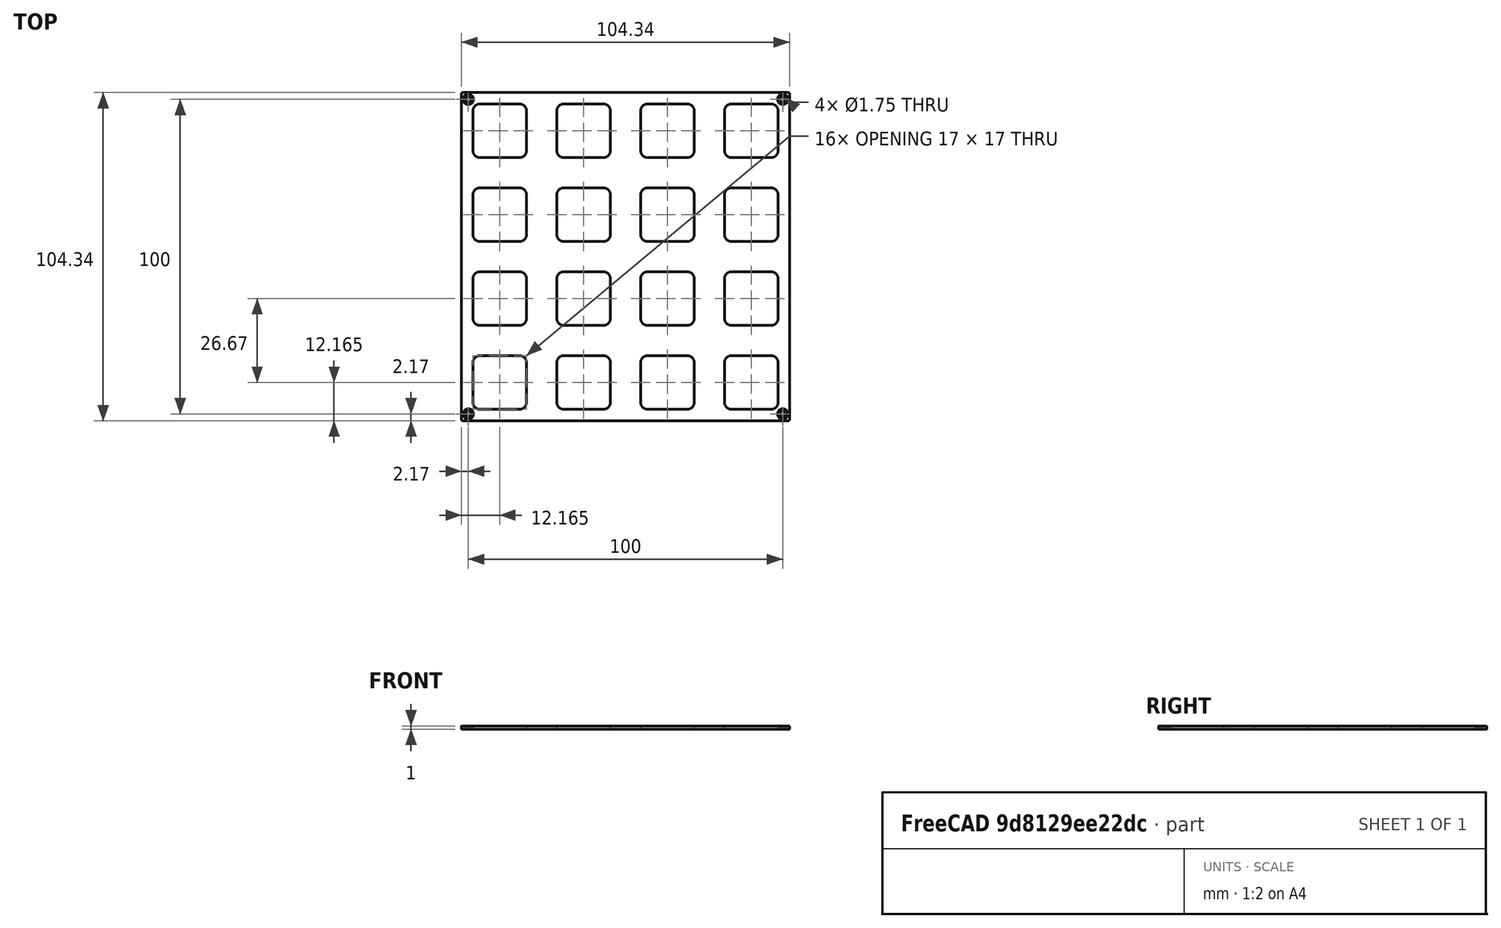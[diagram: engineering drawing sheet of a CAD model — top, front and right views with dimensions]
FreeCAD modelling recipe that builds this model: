
FCSTD DOCUMENT  (FreeCAD 1.0R39109 (Git))
Label: FRONTPANEL-SHEET-BU16 - VSN
License: All rights reserved
LicenseURL: https://en.wikipedia.org/wiki/All_rights_reserved
objects: TechDraw::DrawViewBalloon×13, TechDraw::DrawViewDimension×8, Sketcher::SketchObject×7, TechDraw::DrawHatch×7, TechDraw::DrawViewPart×5, TechDraw::DrawViewAnnotation×3, TechDraw::DrawSVGTemplate×2, PartDesign::Pocket×2, PartDesign::Body×2, TechDraw::DrawPage×2, Spreadsheet::Sheet×1, PartDesign::Pad×1, PartDesign::Hole×1, PartDesign::FeatureBase×1, TechDraw::DrawComplexSection×1
note: 41 computed .brp shape members not serialized (recipe doc carries the construction recipe); baked Part::Feature solids carry a one-line shape summary decoded from their .brp

FEATURE [TechDraw::DrawSVGTemplate] Template003
  EditableTexts = COLOR=Anodized matte black - RAL code: 9004; CreationDate=2024/05/14; E.G.APPROVED=APPROVED; FC-Scale=1:1; FC-Title=BU16 - frontpanel; IntechStudioLtd.=Intech Studio Ltd.; MATERIAL=Aluminum 5052-H32; REV=03; STANDARD=ISO 2768 - m
  Height = 297
  Orientation = 1
  Template = <userpath>/Desktop/A3_LandscapeTD_MODIFIED.svg
  Width = 420
FEATURE [Spreadsheet::Sheet] Spreadsheet  label="dim"
  cells = A1='panel_length; B1(panel_length)=104.35; A2='panel_thickness; B2(panel_thickness)=1; A3='panel_radius; B3(panel_radius)==(104.35 - 103.6) / 2; A5='corner_drill_dist; B5(corner_drill_dist)=100; A6='corner_drill_dia; B6(corner_drill_dia)=1.75; A7='corner_drill_countersink; B7(corner_drill_countersink)=3.3; A9='undercut_width; B9(undercut_width)=1; A10='undercut_length; B10(undercut_length)=90; A11='undercut_offset; B11(undercut_offset)=1; A12='undercut_depth; B12(undercut_depth)=0.8; A14='ui_raster; B14(ui_raster)=26.67; A16='light_drill_dia; B16(light_drill_dia)=3; D16='old 2.9; A17='light_bore_dia; B17(light_bore_dia)=3.45; C17='check; D17='old 3.30; E17='DEPRICATED; A18='light_bore_depth; B18(light_bore_depth)=0.4; C18='check; D18='old 0.40; E18='DEPRICATED; A20='pot_drill_dia; B20(pot_drill_dia)=9.7; C20='check; D20='old 6.20; A21='pot_led_dist; B21(pot_led_dist)=8.5; B22=0; A23='but_drill_dia; B23(but_drill_dia)=9.8; A24='but_led_dist; B24(but_led_dist)=8.5; A26='fad_cutout_width; B26(fad_cutout_width)=2; C26='check; D26='old 1.50; A27='fad_cutout_length; B27(fad_cutout_length)=36; A28='fad_led_dist; B28(fad_led_dist)=25; A30='enc_drill_dia; B30(enc_drill_dia)=9.7; C30='check; D30='old 6.20; A31='enc_led_dist; B31(enc_led_dist)=8.5; A33='longfad_cutout_width; B33(longfad_cutout_width)=2; A34='longfad_cutout_length; B34(longfad_cutout_length)=66; A36='panel_chamfer; B36(panel_chamfer)=0.2; C36='UPDATE DRAWING
FEATURE [Sketcher::SketchObject] Sketch006
  ArcFitTolerance = 0
  AttachmentSupport = -> [XY_Plane002]
  FullyConstrained = true
  MakeInternals = false
  MapMode = 5
  expr: Constraints[4] = <<dim>>.ui_raster
  expr: Constraints[84] = <<dim>>.but_led_dist
  sketch-geometry (34):
    g0: Circle CenterX=-40.005 CenterY=48.505 CenterZ=0 NormalX=0 NormalY=0 NormalZ=1 AngleXU=0 Radius=2
    g1: Circle CenterX=-13.335 CenterY=48.505 CenterZ=0 NormalX=0 NormalY=0 NormalZ=1 AngleXU=0 Radius=2
    g2: LineSegment [constr] StartX=-40.005 StartY=48.505 StartZ=0 EndX=-13.335 EndY=48.505 EndZ=0
    g3: Circle CenterX=13.335 CenterY=48.505 CenterZ=0 NormalX=0 NormalY=0 NormalZ=1 AngleXU=0 Radius=2
    g4: LineSegment [constr] StartX=-13.335 StartY=48.505 StartZ=0 EndX=13.335 EndY=48.505 EndZ=0
    g5: Circle CenterX=40.005 CenterY=48.505 CenterZ=0 NormalX=0 NormalY=0 NormalZ=1 AngleXU=0 Radius=2
    g6: LineSegment [constr] StartX=13.335 StartY=48.505 StartZ=0 EndX=40.005 EndY=48.505 EndZ=0
    g7: Circle CenterX=-40.005 CenterY=21.835 CenterZ=0 NormalX=0 NormalY=0 NormalZ=1 AngleXU=0 Radius=2
    g8: LineSegment [constr] StartX=-40.005 StartY=48.505 StartZ=0 EndX=-40.005 EndY=21.835 EndZ=0
    g9: Circle CenterX=-13.335 CenterY=21.835 CenterZ=0 NormalX=0 NormalY=0 NormalZ=1 AngleXU=0 Radius=2
    g10: LineSegment [constr] StartX=-40.005 StartY=21.835 StartZ=0 EndX=-13.335 EndY=21.835 EndZ=0
    g11: Circle CenterX=13.335 CenterY=21.835 CenterZ=0 NormalX=0 NormalY=0 NormalZ=1 AngleXU=0 Radius=2
    g12: LineSegment [constr] StartX=-13.335 StartY=21.835 StartZ=0 EndX=13.335 EndY=21.835 EndZ=0
    g13: Circle CenterX=40.005 CenterY=21.835 CenterZ=0 NormalX=0 NormalY=0 NormalZ=1 AngleXU=0 Radius=2
    g14: LineSegment [constr] StartX=13.335 StartY=21.835 StartZ=0 EndX=40.005 EndY=21.835 EndZ=0
    g15: Circle CenterX=-40.005 CenterY=-4.835 CenterZ=0 NormalX=0 NormalY=0 NormalZ=1 AngleXU=0 Radius=2
    g16: LineSegment [constr] StartX=-40.005 StartY=21.835 StartZ=0 EndX=-40.005 EndY=-4.835 EndZ=0
    g17: Circle CenterX=-13.335 CenterY=-4.835 CenterZ=0 NormalX=0 NormalY=0 NormalZ=1 AngleXU=0 Radius=2
    g18: LineSegment [constr] StartX=-40.005 StartY=-4.835 StartZ=0 EndX=-13.335 EndY=-4.835 EndZ=0
    g19: Circle CenterX=13.335 CenterY=-4.835 CenterZ=0 NormalX=0 NormalY=0 NormalZ=1 AngleXU=0 Radius=2
    g20: LineSegment [constr] StartX=-13.335 StartY=-4.835 StartZ=0 EndX=13.335 EndY=-4.835 EndZ=0
    g21: Circle CenterX=40.005 CenterY=-4.835 CenterZ=0 NormalX=0 NormalY=0 NormalZ=1 AngleXU=0 Radius=2
    g22: LineSegment [constr] StartX=13.335 StartY=-4.835 StartZ=0 EndX=40.005 EndY=-4.835 EndZ=0
    g23: Circle CenterX=-40.005 CenterY=-31.505 CenterZ=0 NormalX=0 NormalY=0 NormalZ=1 AngleXU=0 Radius=2
    g24: LineSegment [constr] StartX=-40.005 StartY=-4.835 StartZ=0 EndX=-40.005 EndY=-31.505 EndZ=0
    g25: Circle CenterX=-13.335 CenterY=-31.505 CenterZ=0 NormalX=0 NormalY=0 NormalZ=1 AngleXU=0 Radius=2
    g26: LineSegment [constr] StartX=-40.005 StartY=-31.505 StartZ=0 EndX=-13.335 EndY=-31.505 EndZ=0
    g27: Circle CenterX=13.335 CenterY=-31.505 CenterZ=0 NormalX=0 NormalY=0 NormalZ=1 AngleXU=0 Radius=2
    g28: LineSegment [constr] StartX=-13.335 StartY=-31.505 StartZ=0 EndX=13.335 EndY=-31.505 EndZ=0
    g29: Circle CenterX=40.005 CenterY=-31.505 CenterZ=0 NormalX=0 NormalY=0 NormalZ=1 AngleXU=0 Radius=2
    g30: LineSegment [constr] StartX=13.335 StartY=-31.505 StartZ=0 EndX=40.005 EndY=-31.505 EndZ=0
    g31: LineSegment [constr] StartX=-13.335 StartY=21.835 StartZ=0 EndX=-1.8e-15 EndY=8.5 EndZ=0
    g32: LineSegment [constr] StartX=-1.8e-15 StartY=8.5 StartZ=0 EndX=13.335 EndY=21.835 EndZ=0
    g33: LineSegment [constr] StartX=-1.8e-15 StartY=8.5 StartZ=0 EndX=-13.335 EndY=-4.835 EndZ=0
  constraints (85):
    c: Diameter(g0) = 4
    c: Diameter(g1) = 4
    c: Coincident(g0,g2)
    c: Coincident(g1,g2)
    c: Distance(g2) = 26.67
    c: Angle(g2) = 0
    c: Diameter(g3) = 4
    c: Coincident(g1,g4)
    c: Coincident(g3,g4)
    c: Equal(g2,g4)
    c: Parallel(g4,g2)
    c: Diameter(g5) = 4
    c: Coincident(g3,g6)
    c: Coincident(g5,g6)
    c: Equal(g2,g6)
    c: Parallel(g6,g2)
    c: Diameter(g7) = 4
    c: Coincident(g0,g8)
    c: Coincident(g7,g8)
    c: Equal(g8,g2)
    c: Perpendicular(g8,g2)
    c: Diameter(g9) = 4
    c: Coincident(g7,g10)
    c: Coincident(g9,g10)
    c: Equal(g2,g10)
    c: Parallel(g10,g2)
    c: Diameter(g11) = 4
    c: Coincident(g9,g12)
    c: Coincident(g11,g12)
    c: Equal(g2,g12)
    c: Parallel(g12,g2)
    c: Diameter(g13) = 4
    c: Coincident(g11,g14)
    c: Coincident(g13,g14)
    c: Equal(g2,g14)
    c: Parallel(g14,g2)
    c: Diameter(g15) = 4
    c: Coincident(g7,g16)
    c: Coincident(g15,g16)
    c: Equal(g8,g16)
    c: Perpendicular(g16,g2)
    c: Diameter(g17) = 4
    c: Coincident(g15,g18)
    c: Coincident(g17,g18)
    c: Equal(g2,g18)
    c: Parallel(g18,g2)
    c: Diameter(g19) = 4
    c: Coincident(g17,g20)
    c: Coincident(g19,g20)
    c: Equal(g2,g20)
    c: Parallel(g20,g2)
    c: Diameter(g21) = 4
    c: Coincident(g19,g22)
    c: Coincident(g21,g22)
    c: Equal(g2,g22)
    c: Parallel(g22,g2)
    c: Diameter(g23) = 4
    c: Coincident(g15,g24)
    c: Coincident(g23,g24)
    c: Equal(g8,g24)
    c: Perpendicular(g24,g2)
    c: Diameter(g25) = 4
    c: Coincident(g23,g26)
    c: Coincident(g25,g26)
    c: Equal(g2,g26)
    c: Parallel(g26,g2)
    c: Diameter(g27) = 4
    c: Coincident(g25,g28)
    c: Coincident(g27,g28)
    c: Equal(g2,g28)
    c: Parallel(g28,g2)
    c: Diameter(g29) = 4
    c: Coincident(g27,g30)
    c: Coincident(g29,g30)
    c: Equal(g2,g30)
    c: Parallel(g30,g2)
    c: Coincident(g31,g9)
    c: PointOnObject(g31,g-2)
    c: Coincident(g31,g32)
    c: Coincident(g32,g11)
    c: Coincident(g31,g33)
    c: Coincident(g33,g17)
    c: Equal(g33,g31)
    c: Equal(g31,g32)
    c: DistanceY(g-1,g31) = 8.5
FEATURE [Sketcher::SketchObject] Sketch005
  ArcFitTolerance = 0
  AttachmentSupport = -> [XY_Plane002]
  FullyConstrained = true
  MakeInternals = false
  MapMode = 5
  expr: Constraints[4] = <<dim>>.ui_raster
  sketch-geometry (34):
    g0: Circle CenterX=-40.005 CenterY=40.005 CenterZ=0 NormalX=0 NormalY=0 NormalZ=1 AngleXU=0 Radius=2
    g1: Circle CenterX=-13.335 CenterY=40.005 CenterZ=0 NormalX=0 NormalY=0 NormalZ=1 AngleXU=0 Radius=2
    g2: LineSegment [constr] StartX=-40.005 StartY=40.005 StartZ=0 EndX=-13.335 EndY=40.005 EndZ=0
    g3: Circle CenterX=13.335 CenterY=40.005 CenterZ=0 NormalX=0 NormalY=0 NormalZ=1 AngleXU=0 Radius=2
    g4: LineSegment [constr] StartX=-13.335 StartY=40.005 StartZ=0 EndX=13.335 EndY=40.005 EndZ=0
    g5: Circle CenterX=40.005 CenterY=40.005 CenterZ=0 NormalX=0 NormalY=0 NormalZ=1 AngleXU=0 Radius=2
    g6: LineSegment [constr] StartX=13.335 StartY=40.005 StartZ=0 EndX=40.005 EndY=40.005 EndZ=0
    g7: Circle CenterX=-40.005 CenterY=13.335 CenterZ=0 NormalX=0 NormalY=0 NormalZ=1 AngleXU=0 Radius=2
    g8: LineSegment [constr] StartX=-40.005 StartY=40.005 StartZ=0 EndX=-40.005 EndY=13.335 EndZ=0
    g9: Circle CenterX=-13.335 CenterY=13.335 CenterZ=0 NormalX=0 NormalY=0 NormalZ=1 AngleXU=0 Radius=2
    g10: LineSegment [constr] StartX=-40.005 StartY=13.335 StartZ=0 EndX=-13.335 EndY=13.335 EndZ=0
    g11: Circle CenterX=13.335 CenterY=13.335 CenterZ=0 NormalX=0 NormalY=0 NormalZ=1 AngleXU=0 Radius=2
    g12: LineSegment [constr] StartX=-13.335 StartY=13.335 StartZ=0 EndX=13.335 EndY=13.335 EndZ=0
    g13: Circle CenterX=40.005 CenterY=13.335 CenterZ=0 NormalX=0 NormalY=0 NormalZ=1 AngleXU=0 Radius=2
    g14: LineSegment [constr] StartX=13.335 StartY=13.335 StartZ=0 EndX=40.005 EndY=13.335 EndZ=0
    g15: Circle CenterX=-40.005 CenterY=-13.335 CenterZ=0 NormalX=0 NormalY=0 NormalZ=1 AngleXU=0 Radius=2
    g16: LineSegment [constr] StartX=-40.005 StartY=13.335 StartZ=0 EndX=-40.005 EndY=-13.335 EndZ=0
    g17: Circle CenterX=-13.335 CenterY=-13.335 CenterZ=0 NormalX=0 NormalY=0 NormalZ=1 AngleXU=0 Radius=2
    g18: LineSegment [constr] StartX=-40.005 StartY=-13.335 StartZ=0 EndX=-13.335 EndY=-13.335 EndZ=0
    g19: Circle CenterX=13.335 CenterY=-13.335 CenterZ=0 NormalX=0 NormalY=0 NormalZ=1 AngleXU=0 Radius=2
    g20: LineSegment [constr] StartX=-13.335 StartY=-13.335 StartZ=0 EndX=13.335 EndY=-13.335 EndZ=0
    g21: Circle CenterX=40.005 CenterY=-13.335 CenterZ=0 NormalX=0 NormalY=0 NormalZ=1 AngleXU=0 Radius=2
    g22: LineSegment [constr] StartX=13.335 StartY=-13.335 StartZ=0 EndX=40.005 EndY=-13.335 EndZ=0
    g23: Circle CenterX=-40.005 CenterY=-40.005 CenterZ=0 NormalX=0 NormalY=0 NormalZ=1 AngleXU=0 Radius=2
    g24: LineSegment [constr] StartX=-40.005 StartY=-13.335 StartZ=0 EndX=-40.005 EndY=-40.005 EndZ=0
    g25: Circle CenterX=-13.335 CenterY=-40.005 CenterZ=0 NormalX=0 NormalY=0 NormalZ=1 AngleXU=0 Radius=2
    g26: LineSegment [constr] StartX=-40.005 StartY=-40.005 StartZ=0 EndX=-13.335 EndY=-40.005 EndZ=0
    g27: Circle CenterX=13.335 CenterY=-40.005 CenterZ=0 NormalX=0 NormalY=0 NormalZ=1 AngleXU=0 Radius=2
    g28: LineSegment [constr] StartX=-13.335 StartY=-40.005 StartZ=0 EndX=13.335 EndY=-40.005 EndZ=0
    g29: Circle CenterX=40.005 CenterY=-40.005 CenterZ=0 NormalX=0 NormalY=0 NormalZ=1 AngleXU=0 Radius=2
    g30: LineSegment [constr] StartX=13.335 StartY=-40.005 StartZ=0 EndX=40.005 EndY=-40.005 EndZ=0
    g31: LineSegment [constr] StartX=-13.335 StartY=13.335 StartZ=0 EndX=-1.8e-15 EndY=0 EndZ=0
    g32: LineSegment [constr] StartX=-1.8e-15 StartY=0 StartZ=0 EndX=13.335 EndY=13.335 EndZ=0
    g33: LineSegment [constr] StartX=0 StartY=0 StartZ=0 EndX=-13.335 EndY=-13.335 EndZ=0
  constraints (84):
    c: Diameter(g0) = 4
    c: Diameter(g1) = 4
    c: Coincident(g0,g2)
    c: Coincident(g1,g2)
    c: Distance(g2) = 26.67
    c: Angle(g2) = 0
    c: Diameter(g3) = 4
    c: Coincident(g1,g4)
    c: Coincident(g3,g4)
    c: Equal(g2,g4)
    c: Parallel(g4,g2)
    c: Diameter(g5) = 4
    c: Coincident(g3,g6)
    c: Coincident(g5,g6)
    c: Equal(g2,g6)
    c: Parallel(g6,g2)
    c: Diameter(g7) = 4
    c: Coincident(g0,g8)
    c: Coincident(g7,g8)
    c: Equal(g8,g2)
    c: Perpendicular(g8,g2)
    c: Diameter(g9) = 4
    c: Coincident(g7,g10)
    c: Coincident(g9,g10)
    c: Equal(g2,g10)
    c: Parallel(g10,g2)
    c: Diameter(g11) = 4
    c: Coincident(g9,g12)
    c: Coincident(g11,g12)
    c: Equal(g2,g12)
    c: Parallel(g12,g2)
    c: Diameter(g13) = 4
    c: Coincident(g11,g14)
    c: Coincident(g13,g14)
    c: Equal(g2,g14)
    c: Parallel(g14,g2)
    c: Diameter(g15) = 4
    c: Coincident(g7,g16)
    c: Coincident(g15,g16)
    c: Equal(g8,g16)
    c: Perpendicular(g16,g2)
    c: Diameter(g17) = 4
    c: Coincident(g15,g18)
    c: Coincident(g17,g18)
    c: Equal(g2,g18)
    c: Parallel(g18,g2)
    c: Diameter(g19) = 4
    c: Coincident(g17,g20)
    c: Coincident(g19,g20)
    c: Equal(g2,g20)
    c: Parallel(g20,g2)
    c: Diameter(g21) = 4
    c: Coincident(g19,g22)
    c: Coincident(g21,g22)
    c: Equal(g2,g22)
    c: Parallel(g22,g2)
    c: Diameter(g23) = 4
    c: Coincident(g15,g24)
    c: Coincident(g23,g24)
    c: Equal(g8,g24)
    c: Perpendicular(g24,g2)
    c: Diameter(g25) = 4
    c: Coincident(g23,g26)
    c: Coincident(g25,g26)
    c: Equal(g2,g26)
    c: Parallel(g26,g2)
    c: Diameter(g27) = 4
    c: Coincident(g25,g28)
    c: Coincident(g27,g28)
    c: Equal(g2,g28)
    c: Parallel(g28,g2)
    c: Diameter(g29) = 4
    c: Coincident(g27,g30)
    c: Coincident(g29,g30)
    c: Equal(g2,g30)
    c: Parallel(g30,g2)
    c: Coincident(g31,g9)
    c: Coincident(g31,g-1)
    c: Coincident(g31,g32)
    c: Coincident(g32,g11)
    c: Coincident(g-1,g33)
    c: Coincident(g33,g17)
    c: Equal(g33,g31)
    c: Equal(g31,g32)
FEATURE [Sketcher::SketchObject] Sketch001
  ArcFitTolerance = 0
  AttachmentSupport = -> [XY_Plane]
  FullyConstrained = true
  MakeInternals = false
  MapMode = 5
  expr: Constraints[13] = <<dim>>.corner_drill_dist
  sketch-geometry (9):
    g0: LineSegment [constr] StartX=-50 StartY=50 StartZ=0 EndX=-50 EndY=-50 EndZ=0
    g1: LineSegment [constr] StartX=-50 StartY=-50 StartZ=0 EndX=50 EndY=-50 EndZ=0
    g2: LineSegment [constr] StartX=50 StartY=-50 StartZ=0 EndX=50 EndY=50 EndZ=0
    g3: LineSegment [constr] StartX=50 StartY=50 StartZ=0 EndX=-50 EndY=50 EndZ=0
    g4: Circle [constr] CenterX=0 CenterY=0 CenterZ=0 NormalX=0 NormalY=0 NormalZ=1 AngleXU=0 Radius=70.7107
    g5: Circle CenterX=-50 CenterY=50 CenterZ=0 NormalX=0 NormalY=0 NormalZ=1 AngleXU=0 Radius=0.5
    g6: Circle CenterX=50 CenterY=50 CenterZ=0 NormalX=0 NormalY=0 NormalZ=1 AngleXU=0 Radius=0.5
    g7: Circle CenterX=50 CenterY=-50 CenterZ=0 NormalX=0 NormalY=0 NormalZ=1 AngleXU=0 Radius=0.5
    g8: Circle CenterX=-50 CenterY=-50 CenterZ=0 NormalX=0 NormalY=0 NormalZ=1 AngleXU=0 Radius=0.5
  constraints (22):
    c: Coincident(g0,g1)
    c: Coincident(g1,g2)
    c: Coincident(g2,g3)
    c: Coincident(g3,g0)
    c: Equal(g0,g1)
    c: Equal(g0,g2)
    c: Equal(g0,g3)
    c: PointOnObject(g0,g4)
    c: PointOnObject(g1,g4)
    c: PointOnObject(g2,g4)
    c: PointOnObject(g3,g4)
    c: Coincident(g4,g-1)
    c: Horizontal(g3)
    c: DistanceX(g3,g3) = 100
    c: Coincident(g5,g0)
    c: Coincident(g6,g2)
    c: Coincident(g7,g1)
    c: Coincident(g8,g0)
    c: Diameter(g8) = 1
    c: Equal(g8,g7)
    c: Equal(g8,g6)
    c: Equal(g8,g5)
FEATURE [Sketcher::SketchObject] Sketch002
  ArcFitTolerance = 0
  AttachmentOffset = pos=(0,0,-4.8) rot=(0,0,1;0rad)
  AttachmentSupport = -> [XY_Plane]
  FullyConstrained = true
  MakeInternals = false
  MapMode = 5
  Placement = pos=(0,0,-4.8) rot=(0,0,1;0rad)
  expr: .AttachmentOffset.Base.z = -<<dim>>.undercut_depth - 4
  expr: Constraints[91] = <<dim>>.undercut_length
  expr: Constraints[92] = <<dim>>.undercut_width
  expr: Constraints[93] = <<dim>>.panel_length / 2 - <<dim>>.undercut_offset - <<dim>>.undercut_width / 2
  sketch-geometry (40):
    g0: LineSegment StartX=-45 StartY=50.175 StartZ=0 EndX=45 EndY=50.175 EndZ=0
    g1: LineSegment StartX=-45 StartY=51.175 StartZ=0 EndX=45 EndY=51.175 EndZ=0
    g2: LineSegment [constr] StartX=-50.675 StartY=45 StartZ=0 EndX=0 EndY=0 EndZ=0
    g3: LineSegment [constr] StartX=0 StartY=0 StartZ=0 EndX=-50.675 EndY=-45 EndZ=0
    g4: LineSegment [constr] StartX=0 StartY=0 StartZ=0 EndX=-45 EndY=50.675 EndZ=0
    g5: LineSegment [constr] StartX=45 StartY=50.675 StartZ=0 EndX=0 EndY=0 EndZ=0
    g6: LineSegment [constr] StartX=0 StartY=0 StartZ=0 EndX=50.675 EndY=45 EndZ=0
    g7: LineSegment [constr] StartX=50.675 StartY=-45 StartZ=0 EndX=0 EndY=0 EndZ=0
    g8: LineSegment [constr] StartX=0 StartY=0 StartZ=0 EndX=45 EndY=-50.675 EndZ=0
    g9: LineSegment [constr] StartX=0 StartY=0 StartZ=0 EndX=-45 EndY=-50.675 EndZ=0
    g10: ArcOfCircle CenterX=45 CenterY=50.675 CenterZ=0 NormalX=0 NormalY=0 NormalZ=1 AngleXU=0 Radius=0.5 StartAngle=4.71239 EndAngle=6.28319
    g11: ArcOfCircle CenterX=45 CenterY=50.675 CenterZ=0 NormalX=0 NormalY=0 NormalZ=1 AngleXU=0 Radius=0.5 StartAngle=0 EndAngle=1.5708
    g12: LineSegment [constr] StartX=45 StartY=50.675 StartZ=0 EndX=45.5 EndY=50.675 EndZ=0
    g13: ArcOfCircle CenterX=-45 CenterY=50.675 CenterZ=0 NormalX=0 NormalY=0 NormalZ=1 AngleXU=0 Radius=0.5 StartAngle=3.14159 EndAngle=4.71239
    g14: ArcOfCircle CenterX=-45 CenterY=50.675 CenterZ=0 NormalX=0 NormalY=0 NormalZ=1 AngleXU=0 Radius=0.5 StartAngle=1.5708 EndAngle=3.14159
    g15: LineSegment [constr] StartX=-45.5 StartY=50.675 StartZ=0 EndX=-45 EndY=50.675 EndZ=0
    g16: LineSegment StartX=-45 StartY=-51.175 StartZ=0 EndX=45 EndY=-51.175 EndZ=0
    g17: LineSegment StartX=-45 StartY=-50.175 StartZ=0 EndX=45 EndY=-50.175 EndZ=0
    g18: ArcOfCircle CenterX=45 CenterY=-50.675 CenterZ=0 NormalX=0 NormalY=0 NormalZ=1 AngleXU=0 Radius=0.5 StartAngle=4.71239 EndAngle=6.28319
    g19: ArcOfCircle CenterX=45 CenterY=-50.675 CenterZ=0 NormalX=0 NormalY=0 NormalZ=1 AngleXU=0 Radius=0.5 StartAngle=0 EndAngle=1.5708
    g20: LineSegment [constr] StartX=45 StartY=-50.675 StartZ=0 EndX=45.5 EndY=-50.675 EndZ=0
    g21: ArcOfCircle CenterX=-45 CenterY=-50.675 CenterZ=0 NormalX=0 NormalY=0 NormalZ=1 AngleXU=0 Radius=0.5 StartAngle=3.14159 EndAngle=4.71239
    g22: ArcOfCircle CenterX=-45 CenterY=-50.675 CenterZ=0 NormalX=0 NormalY=0 NormalZ=1 AngleXU=0 Radius=0.5 StartAngle=1.5708 EndAngle=3.14159
    g23: LineSegment [constr] StartX=-45.5 StartY=-50.675 StartZ=0 EndX=-45 EndY=-50.675 EndZ=0
    g24: LineSegment StartX=51.175 StartY=-45 StartZ=0 EndX=51.175 EndY=45 EndZ=0
    g25: LineSegment StartX=50.175 StartY=-45 StartZ=0 EndX=50.175 EndY=45 EndZ=0
    g26: ArcOfCircle CenterX=50.675 CenterY=45 CenterZ=0 NormalX=0 NormalY=0 NormalZ=1 AngleXU=0 Radius=0.5 StartAngle=3.8e-15 EndAngle=1.5708
    g27: ArcOfCircle CenterX=50.675 CenterY=45 CenterZ=0 NormalX=0 NormalY=0 NormalZ=1 AngleXU=0 Radius=0.5 StartAngle=1.5708 EndAngle=3.14159
    g28: LineSegment [constr] StartX=50.675 StartY=45 StartZ=0 EndX=50.675 EndY=45.5 EndZ=0
    g29: ArcOfCircle CenterX=50.675 CenterY=-45 CenterZ=0 NormalX=0 NormalY=0 NormalZ=1 AngleXU=0 Radius=0.5 StartAngle=4.71239 EndAngle=6.28319
    g30: ArcOfCircle CenterX=50.675 CenterY=-45 CenterZ=0 NormalX=0 NormalY=0 NormalZ=1 AngleXU=0 Radius=0.5 StartAngle=3.14159 EndAngle=4.71239
    g31: LineSegment [constr] StartX=50.675 StartY=-45.5 StartZ=0 EndX=50.675 EndY=-45 EndZ=0
    g32: LineSegment StartX=-50.175 StartY=-45 StartZ=0 EndX=-50.175 EndY=45 EndZ=0
    g33: LineSegment StartX=-51.175 StartY=-45 StartZ=0 EndX=-51.175 EndY=45 EndZ=0
    g34: ArcOfCircle CenterX=-50.675 CenterY=45 CenterZ=0 NormalX=0 NormalY=0 NormalZ=1 AngleXU=0 Radius=0.5 StartAngle=1.4e-15 EndAngle=1.5708
    g35: ArcOfCircle CenterX=-50.675 CenterY=45 CenterZ=0 NormalX=0 NormalY=0 NormalZ=1 AngleXU=0 Radius=0.5 StartAngle=1.5708 EndAngle=3.14159
    g36: LineSegment [constr] StartX=-50.675 StartY=45 StartZ=0 EndX=-50.675 EndY=45.5 EndZ=0
    g37: ArcOfCircle CenterX=-50.675 CenterY=-45 CenterZ=0 NormalX=0 NormalY=0 NormalZ=1 AngleXU=0 Radius=0.5 StartAngle=4.71239 EndAngle=6.28319
    g38: ArcOfCircle CenterX=-50.675 CenterY=-45 CenterZ=0 NormalX=0 NormalY=0 NormalZ=1 AngleXU=0 Radius=0.5 StartAngle=3.14159 EndAngle=4.71239
    g39: LineSegment [constr] StartX=-50.675 StartY=-45.5 StartZ=0 EndX=-50.675 EndY=-45 EndZ=0
  constraints (96):
    c: Horizontal(g0)
    c: Coincident(g2,g-1)
    c: Coincident(g2,g3)
    c: Coincident(g-1,g4)
    c: Coincident(g5,g-1)
    c: Coincident(g5,g6)
    c: Coincident(g7,g-1)
    c: Coincident(g7,g8)
    c: Coincident(g-1,g9)
    c: Equal(g5,g6)
    c: Equal(g6,g8)
    c: Equal(g8,g7)
    c: Equal(g7,g9)
    c: Equal(g9,g3)
    c: Equal(g3,g2)
    c: Equal(g2,g4)
    c: Coincident(g10,g5)
    c: Coincident(g11,g10)
    c: Coincident(g11,g10)
    c: Tangent(g11,g1) = 1.5708
    c: Tangent(g10,g0) = -1.5708
    c: Coincident(g12,g10)
    c: Coincident(g12,g10)
    c: Horizontal(g12)
    c: Coincident(g13,g4)
    c: Coincident(g14,g13)
    c: Coincident(g14,g13)
    c: Tangent(g14,g1) = 1.5708
    c: Tangent(g13,g0) = -1.5708
    c: Coincident(g15,g13)
    c: Coincident(g15,g13)
    c: Horizontal(g15)
    c: Horizontal(g1)
    c: Horizontal(g16)
    c: Coincident(g19,g18)
    c: Coincident(g19,g18)
    c: Tangent(g19,g17) = 1.5708
    c: Tangent(g18,g16) = -1.5708
    c: Coincident(g20,g18)
    c: Coincident(g20,g18)
    c: Horizontal(g20)
    c: Coincident(g22,g21)
    c: Coincident(g22,g21)
    c: Tangent(g22,g17) = 1.5708
    c: Tangent(g21,g16) = -1.5708
    c: Coincident(g23,g21)
    c: Coincident(g23,g21)
    c: Horizontal(g23)
    c: Horizontal(g17)
    c: Coincident(g21,g9)
    c: Coincident(g8,g18)
    c: Equal(g22,g14)
    c: Equal(g17,g1)
    c: Coincident(g27,g26)
    c: Coincident(g27,g26)
    c: Tangent(g27,g25) = 1.5708
    c: Tangent(g26,g24) = -1.5708
    c: Coincident(g28,g26)
    c: Coincident(g28,g26)
    c: Coincident(g30,g29)
    c: Coincident(g30,g29)
    c: Tangent(g30,g25) = 1.5708
    c: Tangent(g29,g24) = -1.5708
    c: Coincident(g31,g29)
    c: Coincident(g31,g29)
    c: Vertical(g31)
    c: Vertical(g28)
    c: Vertical(g25)
    c: Vertical(g24)
    c: Coincident(g35,g34)
    c: Coincident(g35,g34)
    c: Tangent(g35,g33) = 1.5708
    c: Tangent(g34,g32) = -1.5708
    c: Coincident(g36,g34)
    c: Coincident(g36,g34)
    c: Coincident(g38,g37)
    c: Coincident(g38,g37)
    c: Tangent(g38,g33) = 1.5708
    c: Tangent(g37,g32) = -1.5708
    c: Coincident(g39,g37)
    c: Coincident(g39,g37)
    c: Vertical(g39)
    c: Vertical(g36)
    c: Vertical(g33)
    c: Vertical(g32)
    c: Coincident(g6,g26)
    c: Coincident(g7,g29)
    c: Equal(g25,g0)
    c: Equal(g11,g27)
    c: Equal(g1,g33)
    c: Equal(g35,g11)
    c: DistanceX(g13,g10) = 90
    c: Diameter(g13) = 1
    c: DistanceY(g-1,g13) = 50.675
    c: Coincident(g2,g34)
    c: Coincident(g3,g37)
FEATURE [Sketcher::SketchObject] Sketch
  ArcFitTolerance = 0
  AttachmentSupport = -> [XY_Plane]
  FullyConstrained = true
  MakeInternals = false
  MapMode = 5
  expr: Constraints[12] = <<dim>>.panel_radius
  expr: Constraints[16] = <<dim>>.panel_length
  sketch-geometry (11):
    g0: LineSegment StartX=-51.8 StartY=52.175 StartZ=0 EndX=51.8 EndY=52.175 EndZ=0
    g1: LineSegment StartX=52.175 StartY=51.8 StartZ=0 EndX=52.175 EndY=-51.8 EndZ=0
    g2: LineSegment StartX=51.8 StartY=-52.175 StartZ=0 EndX=-51.8 EndY=-52.175 EndZ=0
    g3: LineSegment StartX=-52.175 StartY=-51.8 StartZ=0 EndX=-52.175 EndY=51.8 EndZ=0
    g4: ArcOfCircle CenterX=-51.8 CenterY=51.8 CenterZ=0 NormalX=0 NormalY=0 NormalZ=1 AngleXU=0 Radius=0.375 StartAngle=1.5708 EndAngle=3.14159
    g5: ArcOfCircle CenterX=51.8 CenterY=51.8 CenterZ=0 NormalX=0 NormalY=0 NormalZ=1 AngleXU=0 Radius=0.375 StartAngle=8.4e-15 EndAngle=1.5708
    g6: ArcOfCircle CenterX=51.8 CenterY=-51.8 CenterZ=0 NormalX=0 NormalY=0 NormalZ=1 AngleXU=0 Radius=0.375 StartAngle=4.71239 EndAngle=6.28319
    g7: ArcOfCircle CenterX=-51.8 CenterY=-51.8 CenterZ=0 NormalX=0 NormalY=0 NormalZ=1 AngleXU=0 Radius=0.375 StartAngle=3.14159 EndAngle=4.71239
    g8: LineSegment [constr] StartX=-51.8 StartY=51.8 StartZ=0 EndX=0 EndY=0 EndZ=0
    g9: LineSegment [constr] StartX=0 StartY=0 StartZ=0 EndX=51.8 EndY=51.8 EndZ=0
    g10: LineSegment [constr] StartX=0 StartY=0 StartZ=0 EndX=-51.8 EndY=-51.8 EndZ=0
  constraints (26):
    c: Horizontal(g0)
    c: Horizontal(g2)
    c: Vertical(g1)
    c: Vertical(g3)
    c: Tangent(g3,g4) = 1.5708
    c: Tangent(g0,g4) = 1.5708
    c: Tangent(g0,g5) = 1.5708
    c: Tangent(g1,g5) = 1.5708
    c: Tangent(g1,g6) = 1.5708
    c: Tangent(g2,g6) = 1.5708
    c: Tangent(g2,g7) = 1.5708
    c: Tangent(g3,g7) = 1.5708
    c: Radius(g4) = 0.375
    c: Equal(g4,g5)
    c: Equal(g4,g6)
    c: Equal(g4,g7)
    c: DistanceX(g3,g1) = 104.35
    c: Equal(g3,g0)
    c: Coincident(g8,g4)
    c: Coincident(g8,g-1)
    c: Coincident(g8,g9)
    c: Coincident(g9,g5)
    c: Coincident(g-1,g10)
    c: Coincident(g10,g7)
    c: Equal(g10,g8)
    c: Equal(g8,g9)
FEATURE [PartDesign::Pad] Pad  label="panel"
  AllowMultiFace = false
  Direction = (0,0,1)
  Length = 1
  Length2 = 100
  Profile = -> Sketch
  Reversed = true
  Suppressed = false
  Type = 0
  expr: Length = <<dim>>.panel_thickness
FEATURE [PartDesign::Pocket] Pocket
  AllowMultiFace = false
  BaseFeature = -> Pad
  Direction = (0,0,-1)
  Length = 5
  Length2 = 100
  Profile = -> Sketch002
  Suppressed = false
  Type = 1
FEATURE [PartDesign::Hole] Hole
  BaseFeature = -> Pocket
  CustomThreadClearance = 0
  Depth = 298.105
  DepthType = 1
  Diameter = 1.75
  DrillForDepth = false
  DrillPoint = 1
  DrillPointAngle = 118
  HoleCutCountersinkAngle = 90
  HoleCutCustomValues = false
  HoleCutDepth = 0
  HoleCutDiameter = 3.3
  HoleCutType = 2
  ModelThread = false
  Profile = -> Sketch001
  Suppressed = false
  Tapered = false
  TaperedAngle = 90
  ThreadClass = 0
  ThreadDepth = 298.105
  ThreadDepthType = 0
  ThreadDirection = 0
  ThreadFit = 0
  ThreadSize = 0
  ThreadType = 0
  Threaded = false
  UseCustomThreadClearance = false
  expr: Diameter = <<dim>>.corner_drill_dia
  expr: HoleCutDiameter = <<dim>>.corner_drill_countersink
FEATURE [PartDesign::Body] Body  label="Base"
  AllowCompound = false
  Group = -> [Sketch,Pad,Sketch001,Sketch002,Pocket,Hole]
  Origin = -> Origin
  Tip = -> Hole
FEATURE [PartDesign::FeatureBase] Clone001
  BaseFeature = -> Body
  Suppressed = false
FEATURE [TechDraw::DrawViewAnnotation] Annotation
  Font = osifont
  LineSpace = 100
  LockPosition = false
  MaxWidth = -1
  Rotation = 0
  ScaleType = 0
  Text = 10:1
  TextSize = 4
  TextStyle = 0
  X = 76.4884
  Y = 42.7227
FEATURE [TechDraw::DrawViewAnnotation] Annotation001
  Font = osifont
  LineSpace = 100
  LockPosition = false
  MaxWidth = -1
  Rotation = 0
  ScaleType = 0
  Text = 1:2
  TextSize = 4
  TextStyle = 0
  X = 380.038
  Y = 120.843
FEATURE [Sketcher::SketchObject] Sketch007  label="Section A-A"
  ArcFitTolerance = 0
  AttachmentSupport = -> [XY_Plane002]
  FullyConstrained = true
  MakeInternals = false
  MapMode = 5
  sketch-geometry (2):
    g0: LineSegment StartX=-53.5 StartY=-50 StartZ=0 EndX=-46.5 EndY=-50 EndZ=0
    g1: GeomPoint X=-50 Y=-50 Z=0
  constraints (5):
    c: Horizontal(g0)
    c: DistanceX(g0,g0) = 7
    c: Symmetric(g0,g0,g1)
    c: DistanceY(g1,g-1) = 50
    c: DistanceX(g1,g-1) = 50
FEATURE [TechDraw::DrawViewAnnotation] Annotation002
  Font = osifont
  LineSpace = 100
  LockPosition = false
  MaxWidth = -1
  Rotation = 0
  ScaleType = 0
  Text = The mid of the datum plane A is preferred to be near | to the lower limit of the flatness tolerance zone. | It can be achieved with an additional bending step. | Aesthetical surfaces colored red on the view | No scratches, burrs or any kind of damage allowed! | Functional surfaces colored blue on the view (all which perpendicular to the aesthetical) | No burrs or other protruding material allowed!
  TextSize = 3
  TextStyle = 0
  X = 297.303
  Y = 101.437
FEATURE [TechDraw::DrawSVGTemplate] Template
  Height = 210
  Orientation = 1
  Template = C:/Program Files/FreeCAD 0.21/data/Mod/TechDraw/Templates/A4_Landscape_blank.svg
  Width = 297
FEATURE [TechDraw::DrawViewPart] View005
  CoarseView = false
  Direction = (0,0,1)
  Focus = 100
  HardHidden = false
  IsoCount = 0
  IsoHidden = false
  IsoVisible = true
  LockPosition = false
  Perspective = false
  Rotation = 0
  ScaleType = 0
  ScrubCount = 0
  SeamHidden = false
  SeamVisible = true
  SmoothHidden = false
  SmoothVisible = true
  X = 148.5
  XDirection = (1,0,0)
  Y = 105
FEATURE [TechDraw::DrawPage] Page  label="BU16_dxf"
  KeepUpdated = true
  NextBalloonIndex = 1
  ProjectionType = 0
  Template = -> Template
  Views = -> [View005]
FEATURE [TechDraw::DrawViewBalloon] Balloon026
  BubbleShape = 2
  EndType = 6
  EndTypeScale = 1
  KinkLength = 0
  LockPosition = false
  OriginX = -97.7934
  OriginY = -2.76733
  Rotation = 0
  ScaleType = 0
  ShapeScale = 1
  SourceView = -> Annotation002
  Text = 3
  TextWrapLen = -1
  X = -94.5881
  Y = -3.56147
FEATURE [Sketcher::SketchObject] Sketch008
  ArcFitTolerance = 1e-06
  AttachmentSupport = -> [XY_Plane002]
  FullyConstrained = true
  MakeInternals = false
  MapMode = 5
  sketch-geometry (264):
    g0: LineSegment StartX=33.605 StartY=31.505 StartZ=0 EndX=46.405 EndY=31.505 EndZ=0
    g1: LineSegment StartX=48.505 StartY=33.605 StartZ=0 EndX=48.505 EndY=46.405 EndZ=0
    g2: LineSegment StartX=46.405 StartY=48.505 StartZ=0 EndX=33.605 EndY=48.505 EndZ=0
    g3: LineSegment StartX=31.505 StartY=46.405 StartZ=0 EndX=31.505 EndY=33.605 EndZ=0
    g4: ArcOfCircle CenterX=33.605 CenterY=46.405 CenterZ=0 NormalX=0 NormalY=0 NormalZ=1 AngleXU=0 Radius=2.1 StartAngle=1.5708 EndAngle=3.14159
    g5: GeomPoint [constr] X=31.505 Y=48.505 Z=0
    g6: ArcOfCircle CenterX=46.405 CenterY=33.605 CenterZ=0 NormalX=0 NormalY=0 NormalZ=1 AngleXU=0 Radius=2.1 StartAngle=4.71239 EndAngle=6.28319
    g7: GeomPoint [constr] X=48.505 Y=31.505 Z=0
    g8: ArcOfCircle CenterX=46.405 CenterY=46.405 CenterZ=0 NormalX=0 NormalY=0 NormalZ=1 AngleXU=0 Radius=2.1 StartAngle=9e-16 EndAngle=1.5708
    g9: GeomPoint [constr] X=48.505 Y=48.505 Z=0
    g10: ArcOfCircle CenterX=33.605 CenterY=33.605 CenterZ=0 NormalX=0 NormalY=0 NormalZ=1 AngleXU=0 Radius=2.1 StartAngle=3.14159 EndAngle=4.71239
    g11: GeomPoint [constr] X=31.505 Y=31.505 Z=0
    g12: GeomPoint X=40.005 Y=40.005 Z=0
    g13: LineSegment [constr] StartX=40.005 StartY=48.505 StartZ=0 EndX=40.005 EndY=31.505 EndZ=0
    g14: LineSegment [constr] StartX=31.505 StartY=40.005 StartZ=0 EndX=48.505 EndY=40.005 EndZ=0
    g15: LineSegment [constr] StartX=-40.005 StartY=13.335 StartZ=0 EndX=-13.335 EndY=13.335 EndZ=0
    g16: LineSegment [constr] StartX=-13.335 StartY=13.335 StartZ=0 EndX=-13.335 EndY=40.005 EndZ=0
    g17: LineSegment [constr] StartX=-13.335 StartY=40.005 StartZ=0 EndX=-40.005 EndY=40.005 EndZ=0
    g18: LineSegment [constr] StartX=-40.005 StartY=40.005 StartZ=0 EndX=-40.005 EndY=13.335 EndZ=0
    g19: LineSegment [constr] StartX=13.335 StartY=13.335 StartZ=0 EndX=40.005 EndY=13.335 EndZ=0
    g20: LineSegment [constr] StartX=40.005 StartY=13.335 StartZ=0 EndX=40.005 EndY=40.005 EndZ=0
    g21: LineSegment [constr] StartX=40.005 StartY=40.005 StartZ=0 EndX=13.335 EndY=40.005 EndZ=0
    g22: LineSegment [constr] StartX=13.335 StartY=40.005 StartZ=0 EndX=13.335 EndY=13.335 EndZ=0
    g23: LineSegment [constr] StartX=-13.335 StartY=40.005 StartZ=0 EndX=13.335 EndY=40.005 EndZ=0
    g24: LineSegment [constr] StartX=13.335 StartY=13.335 StartZ=0 EndX=-13.335 EndY=13.335 EndZ=0
    g25: LineSegment [constr] StartX=-40.005 StartY=-13.335 StartZ=0 EndX=-40.005 EndY=-40.005 EndZ=0
    g26: LineSegment [constr] StartX=-40.005 StartY=-40.005 StartZ=0 EndX=-13.335 EndY=-40.005 EndZ=0
    g27: LineSegment [constr] StartX=-13.335 StartY=-40.005 StartZ=0 EndX=-13.335 EndY=-13.335 EndZ=0
    g28: LineSegment [constr] StartX=-13.335 StartY=-13.335 StartZ=0 EndX=-40.005 EndY=-13.335 EndZ=0
    g29: LineSegment [constr] StartX=13.335 StartY=-13.335 StartZ=0 EndX=13.335 EndY=-40.005 EndZ=0
    g30: LineSegment [constr] StartX=13.335 StartY=-40.005 StartZ=0 EndX=40.005 EndY=-40.005 EndZ=0
    g31: LineSegment [constr] StartX=40.005 StartY=-40.005 StartZ=0 EndX=40.005 EndY=-13.335 EndZ=0
    g32: LineSegment [constr] StartX=40.005 StartY=-13.335 StartZ=0 EndX=13.335 EndY=-13.335 EndZ=0
    g33: LineSegment [constr] StartX=-40.005 StartY=13.335 StartZ=0 EndX=-40.005 EndY=-13.335 EndZ=0
    g34: LineSegment [constr] StartX=-13.335 StartY=13.335 StartZ=0 EndX=-13.335 EndY=-13.335 EndZ=0
    g35: LineSegment [constr] StartX=-13.335 StartY=-13.335 StartZ=0 EndX=13.335 EndY=-13.335 EndZ=0
    g36: LineSegment [constr] StartX=13.335 StartY=13.335 StartZ=0 EndX=13.335 EndY=-13.335 EndZ=0
    g37: LineSegment [constr] StartX=40.005 StartY=13.335 StartZ=0 EndX=40.005 EndY=-13.335 EndZ=0
    g38: LineSegment [constr] StartX=13.335 StartY=-40.005 StartZ=0 EndX=-13.335 EndY=-40.005 EndZ=0
    g39: LineSegment StartX=-19.735 StartY=31.505 StartZ=0 EndX=-6.935 EndY=31.505 EndZ=0
    g40: LineSegment StartX=-4.835 StartY=33.605 StartZ=0 EndX=-4.835 EndY=46.405 EndZ=0
    g41: LineSegment StartX=-6.935 StartY=48.505 StartZ=0 EndX=-19.735 EndY=48.505 EndZ=0
    g42: LineSegment StartX=-21.835 StartY=46.405 StartZ=0 EndX=-21.835 EndY=33.605 EndZ=0
    g43: ArcOfCircle CenterX=-19.735 CenterY=46.405 CenterZ=0 NormalX=0 NormalY=0 NormalZ=1 AngleXU=0 Radius=2.1 StartAngle=1.5708 EndAngle=3.14159
    g44: GeomPoint [constr] X=-21.835 Y=48.505 Z=0
    g45: ArcOfCircle CenterX=-6.935 CenterY=33.605 CenterZ=0 NormalX=0 NormalY=0 NormalZ=1 AngleXU=0 Radius=2.1 StartAngle=4.71239 EndAngle=6.28319
    g46: GeomPoint [constr] X=-4.835 Y=31.505 Z=0
    g47: ArcOfCircle CenterX=-6.935 CenterY=46.405 CenterZ=0 NormalX=0 NormalY=0 NormalZ=1 AngleXU=0 Radius=2.1 StartAngle=-9e-16 EndAngle=1.5708
    g48: GeomPoint [constr] X=-4.835 Y=48.505 Z=0
    g49: ArcOfCircle CenterX=-19.735 CenterY=33.605 CenterZ=0 NormalX=0 NormalY=0 NormalZ=1 AngleXU=0 Radius=2.1 StartAngle=3.14159 EndAngle=4.71239
    g50: GeomPoint [constr] X=-21.835 Y=31.505 Z=0
    g51: GeomPoint X=-13.335 Y=40.005 Z=0
    g52: LineSegment [constr] StartX=-13.335 StartY=48.505 StartZ=0 EndX=-13.335 EndY=31.505 EndZ=0
    g53: LineSegment [constr] StartX=-21.835 StartY=40.005 StartZ=0 EndX=-4.835 EndY=40.005 EndZ=0
    g54: LineSegment StartX=6.935 StartY=31.505 StartZ=0 EndX=19.735 EndY=31.505 EndZ=0
    g55: LineSegment StartX=21.835 StartY=33.605 StartZ=0 EndX=21.835 EndY=46.405 EndZ=0
    g56: LineSegment StartX=19.735 StartY=48.505 StartZ=0 EndX=6.935 EndY=48.505 EndZ=0
    g57: LineSegment StartX=4.835 StartY=46.405 StartZ=0 EndX=4.835 EndY=33.605 EndZ=0
    g58: ArcOfCircle CenterX=6.935 CenterY=46.405 CenterZ=0 NormalX=0 NormalY=0 NormalZ=1 AngleXU=0 Radius=2.1 StartAngle=1.5708 EndAngle=3.14159
    g59: GeomPoint [constr] X=4.835 Y=48.505 Z=0
    g60: ArcOfCircle CenterX=19.735 CenterY=33.605 CenterZ=0 NormalX=0 NormalY=0 NormalZ=1 AngleXU=0 Radius=2.1 StartAngle=4.71239 EndAngle=6.28319
    g61: GeomPoint [constr] X=21.835 Y=31.505 Z=0
    g62: ArcOfCircle CenterX=19.735 CenterY=46.405 CenterZ=0 NormalX=0 NormalY=0 NormalZ=1 AngleXU=0 Radius=2.1 StartAngle=2e-16 EndAngle=1.5708
    g63: GeomPoint [constr] X=21.835 Y=48.505 Z=0
    g64: ArcOfCircle CenterX=6.935 CenterY=33.605 CenterZ=0 NormalX=0 NormalY=0 NormalZ=1 AngleXU=0 Radius=2.1 StartAngle=3.14159 EndAngle=4.71239
    g65: GeomPoint [constr] X=4.835 Y=31.505 Z=0
    g66: GeomPoint X=13.335 Y=40.005 Z=0
    g67: LineSegment [constr] StartX=13.335 StartY=48.505 StartZ=0 EndX=13.335 EndY=31.505 EndZ=0
    g68: LineSegment [constr] StartX=4.835 StartY=40.005 StartZ=0 EndX=21.835 EndY=40.005 EndZ=0
    g69: LineSegment StartX=33.605 StartY=4.835 StartZ=0 EndX=46.405 EndY=4.835 EndZ=0
    g70: LineSegment StartX=48.505 StartY=6.935 StartZ=0 EndX=48.505 EndY=19.735 EndZ=0
    g71: LineSegment StartX=46.405 StartY=21.835 StartZ=0 EndX=33.605 EndY=21.835 EndZ=0
    g72: LineSegment StartX=31.505 StartY=19.735 StartZ=0 EndX=31.505 EndY=6.935 EndZ=0
    g73: ArcOfCircle CenterX=33.605 CenterY=19.735 CenterZ=0 NormalX=0 NormalY=0 NormalZ=1 AngleXU=0 Radius=2.1 StartAngle=1.5708 EndAngle=3.14159
    g74: GeomPoint [constr] X=31.505 Y=21.835 Z=0
    g75: ArcOfCircle CenterX=46.405 CenterY=6.935 CenterZ=0 NormalX=0 NormalY=0 NormalZ=1 AngleXU=0 Radius=2.1 StartAngle=4.71239 EndAngle=6.28319
    g76: GeomPoint [constr] X=48.505 Y=4.835 Z=0
    g77: ArcOfCircle CenterX=46.405 CenterY=19.735 CenterZ=0 NormalX=0 NormalY=0 NormalZ=1 AngleXU=0 Radius=2.1 StartAngle=4e-16 EndAngle=1.5708
    g78: GeomPoint [constr] X=48.505 Y=21.835 Z=0
    g79: ArcOfCircle CenterX=33.605 CenterY=6.935 CenterZ=0 NormalX=0 NormalY=0 NormalZ=1 AngleXU=0 Radius=2.1 StartAngle=3.14159 EndAngle=4.71239
    g80: GeomPoint [constr] X=31.505 Y=4.835 Z=0
    g81: GeomPoint X=40.005 Y=13.335 Z=0
    g82: LineSegment [constr] StartX=40.005 StartY=21.835 StartZ=0 EndX=40.005 EndY=4.835 EndZ=0
    g83: LineSegment [constr] StartX=31.505 StartY=13.335 StartZ=0 EndX=48.505 EndY=13.335 EndZ=0
    g84: LineSegment StartX=6.935 StartY=4.835 StartZ=0 EndX=19.735 EndY=4.835 EndZ=0
    g85: LineSegment StartX=21.835 StartY=6.935 StartZ=0 EndX=21.835 EndY=19.735 EndZ=0
    g86: LineSegment StartX=19.735 StartY=21.835 StartZ=0 EndX=6.935 EndY=21.835 EndZ=0
    g87: LineSegment StartX=4.835 StartY=19.735 StartZ=0 EndX=4.835 EndY=6.935 EndZ=0
    g88: ArcOfCircle CenterX=6.935 CenterY=19.735 CenterZ=0 NormalX=0 NormalY=0 NormalZ=1 AngleXU=0 Radius=2.1 StartAngle=1.5708 EndAngle=3.14159
    g89: GeomPoint [constr] X=4.835 Y=21.835 Z=0
    g90: ArcOfCircle CenterX=19.735 CenterY=6.935 CenterZ=0 NormalX=0 NormalY=0 NormalZ=1 AngleXU=0 Radius=2.1 StartAngle=4.71239 EndAngle=6.28319
    g91: GeomPoint [constr] X=21.835 Y=4.835 Z=0
    g92: ArcOfCircle CenterX=19.735 CenterY=19.735 CenterZ=0 NormalX=0 NormalY=0 NormalZ=1 AngleXU=0 Radius=2.1 StartAngle=0 EndAngle=1.5708
    g93: GeomPoint [constr] X=21.835 Y=21.835 Z=0
    g94: ArcOfCircle CenterX=6.935 CenterY=6.935 CenterZ=0 NormalX=0 NormalY=0 NormalZ=1 AngleXU=0 Radius=2.1 StartAngle=3.14159 EndAngle=4.71239
    g95: GeomPoint [constr] X=4.835 Y=4.835 Z=0
    g96: GeomPoint X=13.335 Y=13.335 Z=0
    g97: LineSegment [constr] StartX=13.335 StartY=21.835 StartZ=0 EndX=13.335 EndY=4.835 EndZ=0
    g98: LineSegment [constr] StartX=4.835 StartY=13.335 StartZ=0 EndX=21.835 EndY=13.335 EndZ=0
    g99: LineSegment StartX=-19.735 StartY=4.835 StartZ=0 EndX=-6.935 EndY=4.835 EndZ=0
    g100: LineSegment StartX=-4.835 StartY=6.935 StartZ=0 EndX=-4.835 EndY=19.735 EndZ=0
    g101: LineSegment StartX=-6.935 StartY=21.835 StartZ=0 EndX=-19.735 EndY=21.835 EndZ=0
    g102: LineSegment StartX=-21.835 StartY=19.735 StartZ=0 EndX=-21.835 EndY=6.935 EndZ=0
    g103: ArcOfCircle CenterX=-19.735 CenterY=19.735 CenterZ=0 NormalX=0 NormalY=0 NormalZ=1 AngleXU=0 Radius=2.1 StartAngle=1.5708 EndAngle=3.14159
    g104: GeomPoint [constr] X=-21.835 Y=21.835 Z=0
    g105: ArcOfCircle CenterX=-6.935 CenterY=6.935 CenterZ=0 NormalX=0 NormalY=0 NormalZ=1 AngleXU=0 Radius=2.1 StartAngle=4.71239 EndAngle=6.28319
    g106: GeomPoint [constr] X=-4.835 Y=4.835 Z=0
    g107: ArcOfCircle CenterX=-6.935 CenterY=19.735 CenterZ=0 NormalX=0 NormalY=0 NormalZ=1 AngleXU=0 Radius=2.1 StartAngle=0 EndAngle=1.5708
    g108: GeomPoint [constr] X=-4.835 Y=21.835 Z=0
    g109: ArcOfCircle CenterX=-19.735 CenterY=6.935 CenterZ=0 NormalX=0 NormalY=0 NormalZ=1 AngleXU=0 Radius=2.1 StartAngle=3.14159 EndAngle=4.71239
    g110: GeomPoint [constr] X=-21.835 Y=4.835 Z=0
    g111: GeomPoint X=-13.335 Y=13.335 Z=0
    g112: LineSegment [constr] StartX=-13.335 StartY=21.835 StartZ=0 EndX=-13.335 EndY=4.835 EndZ=0
    g113: LineSegment [constr] StartX=-21.835 StartY=13.335 StartZ=0 EndX=-4.835 EndY=13.335 EndZ=0
    g114: LineSegment StartX=-46.405 StartY=4.835 StartZ=0 EndX=-33.605 EndY=4.835 EndZ=0
    g115: LineSegment StartX=-31.505 StartY=6.935 StartZ=0 EndX=-31.505 EndY=19.735 EndZ=0
    g116: LineSegment StartX=-33.605 StartY=21.835 StartZ=0 EndX=-46.405 EndY=21.835 EndZ=0
    g117: LineSegment StartX=-48.505 StartY=19.735 StartZ=0 EndX=-48.505 EndY=6.935 EndZ=0
    g118: ArcOfCircle CenterX=-46.405 CenterY=19.735 CenterZ=0 NormalX=0 NormalY=0 NormalZ=1 AngleXU=0 Radius=2.1 StartAngle=1.5708 EndAngle=3.14159
    g119: GeomPoint [constr] X=-48.505 Y=21.835 Z=0
    g120: ArcOfCircle CenterX=-33.605 CenterY=6.935 CenterZ=0 NormalX=0 NormalY=0 NormalZ=1 AngleXU=0 Radius=2.1 StartAngle=4.71239 EndAngle=6.28319
    g121: GeomPoint [constr] X=-31.505 Y=4.835 Z=0
    g122: ArcOfCircle CenterX=-33.605 CenterY=19.735 CenterZ=0 NormalX=0 NormalY=0 NormalZ=1 AngleXU=0 Radius=2.1 StartAngle=0 EndAngle=1.5708
    g123: GeomPoint [constr] X=-31.505 Y=21.835 Z=0
    g124: ArcOfCircle CenterX=-46.405 CenterY=6.935 CenterZ=0 NormalX=0 NormalY=0 NormalZ=1 AngleXU=0 Radius=2.1 StartAngle=3.14159 EndAngle=4.71239
    g125: GeomPoint [constr] X=-48.505 Y=4.835 Z=0
    g126: GeomPoint X=-40.005 Y=13.335 Z=0
    g127: LineSegment [constr] StartX=-40.005 StartY=21.835 StartZ=0 EndX=-40.005 EndY=4.835 EndZ=0
    g128: LineSegment [constr] StartX=-48.505 StartY=13.335 StartZ=0 EndX=-31.505 EndY=13.335 EndZ=0
    g129: LineSegment StartX=33.605 StartY=-21.835 StartZ=0 EndX=46.405 EndY=-21.835 EndZ=0
    g130: LineSegment StartX=48.505 StartY=-19.735 StartZ=0 EndX=48.505 EndY=-6.935 EndZ=0
    g131: LineSegment StartX=46.405 StartY=-4.835 StartZ=0 EndX=33.605 EndY=-4.835 EndZ=0
    g132: LineSegment StartX=31.505 StartY=-6.935 StartZ=0 EndX=31.505 EndY=-19.735 EndZ=0
    g133: ArcOfCircle CenterX=33.605 CenterY=-6.935 CenterZ=0 NormalX=0 NormalY=0 NormalZ=1 AngleXU=0 Radius=2.1 StartAngle=1.5708 EndAngle=3.14159
    g134: GeomPoint [constr] X=31.505 Y=-4.835 Z=0
    g135: ArcOfCircle CenterX=46.405 CenterY=-19.735 CenterZ=0 NormalX=0 NormalY=0 NormalZ=1 AngleXU=0 Radius=2.1 StartAngle=4.71239 EndAngle=6.28319
    g136: GeomPoint [constr] X=48.505 Y=-21.835 Z=0
    g137: ArcOfCircle CenterX=46.405 CenterY=-6.935 CenterZ=0 NormalX=0 NormalY=0 NormalZ=1 AngleXU=0 Radius=2.1 StartAngle=1e-16 EndAngle=1.5708
    g138: GeomPoint [constr] X=48.505 Y=-4.835 Z=0
    g139: ArcOfCircle CenterX=33.605 CenterY=-19.735 CenterZ=0 NormalX=0 NormalY=0 NormalZ=1 AngleXU=0 Radius=2.1 StartAngle=3.14159 EndAngle=4.71239
    g140: GeomPoint [constr] X=31.505 Y=-21.835 Z=0
    g141: GeomPoint X=40.005 Y=-13.335 Z=0
    g142: LineSegment [constr] StartX=40.005 StartY=-4.835 StartZ=0 EndX=40.005 EndY=-21.835 EndZ=0
    g143: LineSegment [constr] StartX=31.505 StartY=-13.335 StartZ=0 EndX=48.505 EndY=-13.335 EndZ=0
    g144: LineSegment StartX=6.935 StartY=-21.835 StartZ=0 EndX=19.735 EndY=-21.835 EndZ=0
    g145: LineSegment StartX=21.835 StartY=-19.735 StartZ=0 EndX=21.835 EndY=-6.935 EndZ=0
    g146: LineSegment StartX=19.735 StartY=-4.835 StartZ=0 EndX=6.935 EndY=-4.835 EndZ=0
    g147: LineSegment StartX=4.835 StartY=-6.935 StartZ=0 EndX=4.835 EndY=-19.735 EndZ=0
    g148: ArcOfCircle CenterX=6.935 CenterY=-6.935 CenterZ=0 NormalX=0 NormalY=0 NormalZ=1 AngleXU=0 Radius=2.1 StartAngle=1.5708 EndAngle=3.14159
    g149: GeomPoint [constr] X=4.835 Y=-4.835 Z=0
    g150: ArcOfCircle CenterX=19.735 CenterY=-19.735 CenterZ=0 NormalX=0 NormalY=0 NormalZ=1 AngleXU=0 Radius=2.1 StartAngle=4.71239 EndAngle=6.28319
    g151: GeomPoint [constr] X=21.835 Y=-21.835 Z=0
    g152: ArcOfCircle CenterX=19.735 CenterY=-6.935 CenterZ=0 NormalX=0 NormalY=0 NormalZ=1 AngleXU=0 Radius=2.1 StartAngle=2e-16 EndAngle=1.5708
    g153: GeomPoint [constr] X=21.835 Y=-4.835 Z=0
    g154: ArcOfCircle CenterX=6.935 CenterY=-19.735 CenterZ=0 NormalX=0 NormalY=0 NormalZ=1 AngleXU=0 Radius=2.1 StartAngle=3.14159 EndAngle=4.71239
    g155: GeomPoint [constr] X=4.835 Y=-21.835 Z=0
    g156: GeomPoint X=13.335 Y=-13.335 Z=0
    g157: LineSegment [constr] StartX=13.335 StartY=-4.835 StartZ=0 EndX=13.335 EndY=-21.835 EndZ=0
    g158: LineSegment [constr] StartX=4.835 StartY=-13.335 StartZ=0 EndX=21.835 EndY=-13.335 EndZ=0
    g159: LineSegment StartX=-19.735 StartY=-21.835 StartZ=0 EndX=-6.935 EndY=-21.835 EndZ=0
    g160: LineSegment StartX=-4.835 StartY=-19.735 StartZ=0 EndX=-4.835 EndY=-6.935 EndZ=0
    g161: LineSegment StartX=-6.935 StartY=-4.835 StartZ=0 EndX=-19.735 EndY=-4.835 EndZ=0
    g162: LineSegment StartX=-21.835 StartY=-6.935 StartZ=0 EndX=-21.835 EndY=-19.735 EndZ=0
    g163: ArcOfCircle CenterX=-19.735 CenterY=-6.935 CenterZ=0 NormalX=0 NormalY=0 NormalZ=1 AngleXU=0 Radius=2.1 StartAngle=1.5708 EndAngle=3.14159
    g164: GeomPoint [constr] X=-21.835 Y=-4.835 Z=0
    g165: ArcOfCircle CenterX=-6.935 CenterY=-19.735 CenterZ=0 NormalX=0 NormalY=0 NormalZ=1 AngleXU=0 Radius=2.1 StartAngle=4.71239 EndAngle=6.28319
    g166: GeomPoint [constr] X=-4.835 Y=-21.835 Z=0
    g167: ArcOfCircle CenterX=-6.935 CenterY=-6.935 CenterZ=0 NormalX=0 NormalY=0 NormalZ=1 AngleXU=0 Radius=2.1 StartAngle=1e-16 EndAngle=1.5708
    g168: GeomPoint [constr] X=-4.835 Y=-4.835 Z=0
    g169: ArcOfCircle CenterX=-19.735 CenterY=-19.735 CenterZ=0 NormalX=0 NormalY=0 NormalZ=1 AngleXU=0 Radius=2.1 StartAngle=3.14159 EndAngle=4.71239
    g170: GeomPoint [constr] X=-21.835 Y=-21.835 Z=0
    g171: GeomPoint X=-13.335 Y=-13.335 Z=0
    g172: LineSegment [constr] StartX=-13.335 StartY=-4.835 StartZ=0 EndX=-13.335 EndY=-21.835 EndZ=0
    g173: LineSegment [constr] StartX=-21.835 StartY=-13.335 StartZ=0 EndX=-4.835 EndY=-13.335 EndZ=0
    g174: LineSegment StartX=-46.405 StartY=-21.835 StartZ=0 EndX=-33.605 EndY=-21.835 EndZ=0
    g175: LineSegment StartX=-31.505 StartY=-19.735 StartZ=0 EndX=-31.505 EndY=-6.935 EndZ=0
    g176: LineSegment StartX=-33.605 StartY=-4.835 StartZ=0 EndX=-46.405 EndY=-4.835 EndZ=0
    g177: LineSegment StartX=-48.505 StartY=-6.935 StartZ=0 EndX=-48.505 EndY=-19.735 EndZ=0
    g178: ArcOfCircle CenterX=-46.405 CenterY=-6.935 CenterZ=0 NormalX=0 NormalY=0 NormalZ=1 AngleXU=0 Radius=2.1 StartAngle=1.5708 EndAngle=3.14159
    g179: GeomPoint [constr] X=-48.505 Y=-4.835 Z=0
    g180: ArcOfCircle CenterX=-33.605 CenterY=-19.735 CenterZ=0 NormalX=0 NormalY=0 NormalZ=1 AngleXU=0 Radius=2.1 StartAngle=4.71239 EndAngle=6.28319
    g181: GeomPoint [constr] X=-31.505 Y=-21.835 Z=0
    g182: ArcOfCircle CenterX=-33.605 CenterY=-6.935 CenterZ=0 NormalX=0 NormalY=0 NormalZ=1 AngleXU=0 Radius=2.1 StartAngle=0 EndAngle=1.5708
    g183: GeomPoint [constr] X=-31.505 Y=-4.835 Z=0
    g184: ArcOfCircle CenterX=-46.405 CenterY=-19.735 CenterZ=0 NormalX=0 NormalY=0 NormalZ=1 AngleXU=0 Radius=2.1 StartAngle=3.14159 EndAngle=4.71239
    g185: GeomPoint [constr] X=-48.505 Y=-21.835 Z=0
    g186: GeomPoint X=-40.005 Y=-13.335 Z=0
    g187: LineSegment [constr] StartX=-40.005 StartY=-4.835 StartZ=0 EndX=-40.005 EndY=-21.835 EndZ=0
    g188: LineSegment [constr] StartX=-48.505 StartY=-13.335 StartZ=0 EndX=-31.505 EndY=-13.335 EndZ=0
    g189: LineSegment StartX=33.605 StartY=-48.505 StartZ=0 EndX=46.405 EndY=-48.505 EndZ=0
    g190: LineSegment StartX=48.505 StartY=-46.405 StartZ=0 EndX=48.505 EndY=-33.605 EndZ=0
    g191: LineSegment StartX=46.405 StartY=-31.505 StartZ=0 EndX=33.605 EndY=-31.505 EndZ=0
    g192: LineSegment StartX=31.505 StartY=-33.605 StartZ=0 EndX=31.505 EndY=-46.405 EndZ=0
    g193: ArcOfCircle CenterX=33.605 CenterY=-33.605 CenterZ=0 NormalX=0 NormalY=0 NormalZ=1 AngleXU=0 Radius=2.1 StartAngle=1.5708 EndAngle=3.14159
    g194: GeomPoint [constr] X=31.505 Y=-31.505 Z=0
    g195: ArcOfCircle CenterX=46.405 CenterY=-46.405 CenterZ=0 NormalX=0 NormalY=0 NormalZ=1 AngleXU=0 Radius=2.1 StartAngle=4.71239 EndAngle=6.28319
    g196: GeomPoint [constr] X=48.505 Y=-48.505 Z=0
    g197: ArcOfCircle CenterX=46.405 CenterY=-33.605 CenterZ=0 NormalX=0 NormalY=0 NormalZ=1 AngleXU=0 Radius=2.1 StartAngle=1.2e-15 EndAngle=1.5708
    g198: GeomPoint [constr] X=48.505 Y=-31.505 Z=0
    g199: ArcOfCircle CenterX=33.605 CenterY=-46.405 CenterZ=0 NormalX=0 NormalY=0 NormalZ=1 AngleXU=0 Radius=2.1 StartAngle=3.14159 EndAngle=4.71239
    g200: GeomPoint [constr] X=31.505 Y=-48.505 Z=0
    g201: GeomPoint X=40.005 Y=-40.005 Z=0
    g202: LineSegment [constr] StartX=40.005 StartY=-31.505 StartZ=0 EndX=40.005 EndY=-48.505 EndZ=0
    g203: LineSegment [constr] StartX=31.505 StartY=-40.005 StartZ=0 EndX=48.505 EndY=-40.005 EndZ=0
    g204: LineSegment StartX=6.935 StartY=-48.505 StartZ=0 EndX=19.735 EndY=-48.505 EndZ=0
    g205: LineSegment StartX=21.835 StartY=-46.405 StartZ=0 EndX=21.835 EndY=-33.605 EndZ=0
    g206: LineSegment StartX=19.735 StartY=-31.505 StartZ=0 EndX=6.935 EndY=-31.505 EndZ=0
    g207: LineSegment StartX=4.835 StartY=-33.605 StartZ=0 EndX=4.835 EndY=-46.405 EndZ=0
    g208: ArcOfCircle CenterX=6.935 CenterY=-33.605 CenterZ=0 NormalX=0 NormalY=0 NormalZ=1 AngleXU=0 Radius=2.1 StartAngle=1.5708 EndAngle=3.14159
    g209: GeomPoint [constr] X=4.835 Y=-31.505 Z=0
    g210: ArcOfCircle CenterX=19.735 CenterY=-46.405 CenterZ=0 NormalX=0 NormalY=0 NormalZ=1 AngleXU=0 Radius=2.1 StartAngle=4.71239 EndAngle=6.28319
    g211: GeomPoint [constr] X=21.835 Y=-48.505 Z=0
    g212: ArcOfCircle CenterX=19.735 CenterY=-33.605 CenterZ=0 NormalX=0 NormalY=0 NormalZ=1 AngleXU=0 Radius=2.1 StartAngle=5e-16 EndAngle=1.5708
    g213: GeomPoint [constr] X=21.835 Y=-31.505 Z=0
    g214: ArcOfCircle CenterX=6.935 CenterY=-46.405 CenterZ=0 NormalX=0 NormalY=0 NormalZ=1 AngleXU=0 Radius=2.1 StartAngle=3.14159 EndAngle=4.71239
    g215: GeomPoint [constr] X=4.835 Y=-48.505 Z=0
    g216: GeomPoint X=13.335 Y=-40.005 Z=0
    g217: LineSegment [constr] StartX=13.335 StartY=-31.505 StartZ=0 EndX=13.335 EndY=-48.505 EndZ=0
    g218: LineSegment [constr] StartX=4.835 StartY=-40.005 StartZ=0 EndX=21.835 EndY=-40.005 EndZ=0
    g219: LineSegment StartX=-19.735 StartY=-48.505 StartZ=0 EndX=-6.935 EndY=-48.505 EndZ=0
    g220: LineSegment StartX=-4.835 StartY=-46.405 StartZ=0 EndX=-4.835 EndY=-33.605 EndZ=0
    g221: LineSegment StartX=-6.935 StartY=-31.505 StartZ=0 EndX=-19.735 EndY=-31.505 EndZ=0
    g222: LineSegment StartX=-21.835 StartY=-33.605 StartZ=0 EndX=-21.835 EndY=-46.405 EndZ=0
    g223: ArcOfCircle CenterX=-19.735 CenterY=-33.605 CenterZ=0 NormalX=0 NormalY=0 NormalZ=1 AngleXU=0 Radius=2.1 StartAngle=1.5708 EndAngle=3.14159
    g224: GeomPoint [constr] X=-21.835 Y=-31.505 Z=0
    g225: ArcOfCircle CenterX=-6.935 CenterY=-46.405 CenterZ=0 NormalX=0 NormalY=0 NormalZ=1 AngleXU=0 Radius=2.1 StartAngle=4.71239 EndAngle=6.28319
    g226: GeomPoint [constr] X=-4.835 Y=-48.505 Z=0
    g227: ArcOfCircle CenterX=-6.935 CenterY=-33.605 CenterZ=0 NormalX=0 NormalY=0 NormalZ=1 AngleXU=0 Radius=2.1 StartAngle=-9e-16 EndAngle=1.5708
    g228: GeomPoint [constr] X=-4.835 Y=-31.505 Z=0
    g229: ArcOfCircle CenterX=-19.735 CenterY=-46.405 CenterZ=0 NormalX=0 NormalY=0 NormalZ=1 AngleXU=0 Radius=2.1 StartAngle=3.14159 EndAngle=4.71239
    g230: GeomPoint [constr] X=-21.835 Y=-48.505 Z=0
    g231: GeomPoint X=-13.335 Y=-40.005 Z=0
    g232: LineSegment [constr] StartX=-13.335 StartY=-31.505 StartZ=0 EndX=-13.335 EndY=-48.505 EndZ=0
    g233: LineSegment [constr] StartX=-21.835 StartY=-40.005 StartZ=0 EndX=-4.835 EndY=-40.005 EndZ=0
    g234: LineSegment StartX=-46.405 StartY=-48.505 StartZ=0 EndX=-33.605 EndY=-48.505 EndZ=0
    g235: LineSegment StartX=-31.505 StartY=-46.405 StartZ=0 EndX=-31.505 EndY=-33.605 EndZ=0
    g236: LineSegment StartX=-33.605 StartY=-31.505 StartZ=0 EndX=-46.405 EndY=-31.505 EndZ=0
    g237: LineSegment StartX=-48.505 StartY=-33.605 StartZ=0 EndX=-48.505 EndY=-46.405 EndZ=0
    g238: ArcOfCircle CenterX=-46.405 CenterY=-33.605 CenterZ=0 NormalX=0 NormalY=0 NormalZ=1 AngleXU=0 Radius=2.1 StartAngle=1.5708 EndAngle=3.14159
    g239: GeomPoint [constr] X=-48.505 Y=-31.505 Z=0
    g240: ArcOfCircle CenterX=-33.605 CenterY=-46.405 CenterZ=0 NormalX=0 NormalY=0 NormalZ=1 AngleXU=0 Radius=2.1 StartAngle=4.71239 EndAngle=6.28319
    g241: GeomPoint [constr] X=-31.505 Y=-48.505 Z=0
    g242: ArcOfCircle CenterX=-33.605 CenterY=-33.605 CenterZ=0 NormalX=0 NormalY=0 NormalZ=1 AngleXU=0 Radius=2.1 StartAngle=-9e-16 EndAngle=1.5708
    g243: GeomPoint [constr] X=-31.505 Y=-31.505 Z=0
    g244: ArcOfCircle CenterX=-46.405 CenterY=-46.405 CenterZ=0 NormalX=0 NormalY=0 NormalZ=1 AngleXU=0 Radius=2.1 StartAngle=3.14159 EndAngle=4.71239
    g245: GeomPoint [constr] X=-48.505 Y=-48.505 Z=0
    g246: GeomPoint X=-40.005 Y=-40.005 Z=0
    g247: LineSegment [constr] StartX=-40.005 StartY=-31.505 StartZ=0 EndX=-40.005 EndY=-48.505 EndZ=0
    g248: LineSegment [constr] StartX=-48.505 StartY=-40.005 StartZ=0 EndX=-31.505 EndY=-40.005 EndZ=0
    g249: LineSegment StartX=-46.405 StartY=31.505 StartZ=0 EndX=-33.605 EndY=31.505 EndZ=0
    g250: LineSegment StartX=-31.505 StartY=33.605 StartZ=0 EndX=-31.505 EndY=46.405 EndZ=0
    g251: LineSegment StartX=-33.605 StartY=48.505 StartZ=0 EndX=-46.405 EndY=48.505 EndZ=0
    g252: LineSegment StartX=-48.505 StartY=46.405 StartZ=0 EndX=-48.505 EndY=33.605 EndZ=0
    g253: ArcOfCircle CenterX=-46.405 CenterY=46.405 CenterZ=0 NormalX=0 NormalY=0 NormalZ=1 AngleXU=0 Radius=2.1 StartAngle=1.5708 EndAngle=3.14159
    g254: GeomPoint [constr] X=-48.505 Y=48.505 Z=0
    g255: ArcOfCircle CenterX=-33.605 CenterY=33.605 CenterZ=0 NormalX=0 NormalY=0 NormalZ=1 AngleXU=0 Radius=2.1 StartAngle=4.71239 EndAngle=6.28319
    g256: GeomPoint [constr] X=-31.505 Y=31.505 Z=0
    g257: ArcOfCircle CenterX=-33.605 CenterY=46.405 CenterZ=0 NormalX=0 NormalY=0 NormalZ=1 AngleXU=0 Radius=2.1 StartAngle=-1.19362e-11 EndAngle=1.5708
    g258: GeomPoint [constr] X=-31.505 Y=48.505 Z=0
    g259: ArcOfCircle CenterX=-46.405 CenterY=33.605 CenterZ=0 NormalX=0 NormalY=0 NormalZ=1 AngleXU=0 Radius=2.1 StartAngle=3.14159 EndAngle=4.71239
    g260: GeomPoint [constr] X=-48.505 Y=31.505 Z=0
    g261: GeomPoint X=-40.005 Y=40.005 Z=0
    g262: LineSegment [constr] StartX=-40.005 StartY=48.505 StartZ=0 EndX=-40.005 EndY=31.505 EndZ=0
    g263: LineSegment [constr] StartX=-48.505 StartY=40.005 StartZ=0 EndX=-31.505 EndY=40.005 EndZ=0
  constraints (590):
    c: Horizontal(g0)
    c: Horizontal(g2)
    c: Vertical(g1)
    c: Vertical(g3)
    c: PointOnObject(g5,g2)
    c: PointOnObject(g5,g3)
    c: Tangent(g2,g4) = -1.5708
    c: Tangent(g3,g4) = -1.5708
    c: PointOnObject(g7,g1)
    c: PointOnObject(g7,g0)
    c: Tangent(g1,g6) = -1.5708
    c: Tangent(g0,g6) = -1.5708
    c: PointOnObject(g9,g1)
    c: PointOnObject(g9,g2)
    c: Tangent(g1,g8) = -1.5708
    c: Tangent(g2,g8) = -1.5708
    c: PointOnObject(g11,g3)
    c: PointOnObject(g11,g0)
    c: Tangent(g3,g10) = -1.5708
    c: Tangent(g0,g10) = -1.5708
    c: Equal(g10,g4)
    c: Equal(g4,g8)
    c: Equal(g8,g6)
    c: Equal(g1,g2)
    c: Symmetric(g2,g2,g13)
    c: Symmetric(g0,g0,g13)
    c: Symmetric(g3,g3,g14)
    c: Symmetric(g1,g1,g14)
    c: PointOnObject(g12,g13)
    c: PointOnObject(g12,g14)
    c: Coincident(g15,g16)
    c: Coincident(g16,g17)
    c: Coincident(g17,g18)
    c: Coincident(g18,g15)
    c: Horizontal(g15)
    c: Horizontal(g17)
    c: Vertical(g16)
    c: Vertical(g18)
    c: Coincident(g19,g20)
    c: Coincident(g20,g21)
    c: Coincident(g21,g22)
    c: Coincident(g22,g19)
    c: Horizontal(g19)
    c: Horizontal(g21)
    c: Vertical(g20)
    c: Vertical(g22)
    c: Coincident(g23,g16)
    c: Coincident(g23,g21)
    c: Horizontal(g23)
    c: Coincident(g24,g19)
    c: Coincident(g24,g15)
    c: Coincident(g25,g26)
    c: Coincident(g26,g27)
    c: Coincident(g27,g28)
    c: Coincident(g28,g25)
    c: Vertical(g25)
    c: Vertical(g27)
    c: Horizontal(g26)
    c: Horizontal(g28)
    c: Coincident(g29,g30)
    c: Coincident(g30,g31)
    c: Coincident(g31,g32)
    c: Coincident(g32,g29)
    c: Vertical(g29)
    c: Vertical(g31)
    c: Horizontal(g30)
    c: Horizontal(g32)
    c: Coincident(g33,g15)
    c: Coincident(g33,g25)
    c: Coincident(g34,g15)
    c: Coincident(g34,g27)
    c: Vertical(g34)
    c: Coincident(g35,g27)
    c: Coincident(g35,g29)
    c: Horizontal(g35)
    c: Coincident(g36,g19)
    c: Coincident(g36,g29)
    c: Coincident(g37,g19)
    c: Coincident(g37,g31)
    c: Vertical(g37)
    c: Coincident(g38,g29)
    c: Coincident(g38,g26)
    c: Equal(g18,g15)
    c: Vertical(g33)
    c: Horizontal(g38)
    c: Equal(g17,g23)
    c: Equal(g18,g33)
    c: Equal(g33,g25)
    c: Equal(g15,g19)
    c: Symmetric(g19,g15,g-2)
    c: Symmetric(g19,g29,g-1)
    c: DistanceX(g17,g17) = 26.67
    c: Horizontal(g39)
    c: Horizontal(g41)
    c: Vertical(g40)
    c: Vertical(g42)
    c: PointOnObject(g44,g41)
    c: PointOnObject(g44,g42)
    c: Tangent(g41,g43) = -1.5708
    c: Tangent(g42,g43) = -1.5708
    c: PointOnObject(g46,g40)
    c: PointOnObject(g46,g39)
    c: Tangent(g40,g45) = -1.5708
    c: Tangent(g39,g45) = -1.5708
    c: PointOnObject(g48,g40)
    c: PointOnObject(g48,g41)
    c: Tangent(g40,g47) = -1.5708
    c: Tangent(g41,g47) = -1.5708
    c: PointOnObject(g50,g42)
    c: PointOnObject(g50,g39)
    c: Tangent(g42,g49) = -1.5708
    c: Tangent(g39,g49) = -1.5708
    c: Equal(g49,g43)
    c: Equal(g43,g47)
    c: Equal(g47,g45)
    c: Equal(g40,g41)
    c: Symmetric(g41,g41,g52)
    c: Symmetric(g39,g39,g52)
    c: Symmetric(g42,g42,g53)
    c: Symmetric(g40,g40,g53)
    c: PointOnObject(g51,g52)
    c: PointOnObject(g51,g53)
    c: Horizontal(g54)
    c: Horizontal(g56)
    c: Vertical(g55)
    c: Vertical(g57)
    c: PointOnObject(g59,g56)
    c: PointOnObject(g59,g57)
    c: Tangent(g56,g58) = -1.5708
    c: Tangent(g57,g58) = -1.5708
    c: PointOnObject(g61,g55)
    c: PointOnObject(g61,g54)
    c: Tangent(g55,g60) = -1.5708
    c: Tangent(g54,g60) = -1.5708
    c: PointOnObject(g63,g55)
    c: PointOnObject(g63,g56)
    c: Tangent(g55,g62) = -1.5708
    c: Tangent(g56,g62) = -1.5708
    c: PointOnObject(g65,g57)
    c: PointOnObject(g65,g54)
    c: Tangent(g57,g64) = -1.5708
    c: Tangent(g54,g64) = -1.5708
    c: Equal(g64,g58)
    c: Equal(g58,g62)
    c: Equal(g62,g60)
    c: Equal(g55,g56)
    c: Symmetric(g56,g56,g67)
    c: Symmetric(g54,g54,g67)
    c: Symmetric(g57,g57,g68)
    c: Symmetric(g55,g55,g68)
    c: PointOnObject(g66,g67)
    c: PointOnObject(g66,g68)
    c: Horizontal(g69)
    c: Horizontal(g71)
    c: Vertical(g70)
    c: Vertical(g72)
    c: PointOnObject(g74,g71)
    c: PointOnObject(g74,g72)
    c: Tangent(g71,g73) = -1.5708
    c: Tangent(g72,g73) = -1.5708
    c: PointOnObject(g76,g70)
    c: PointOnObject(g76,g69)
    c: Tangent(g70,g75) = -1.5708
    c: Tangent(g69,g75) = -1.5708
    c: PointOnObject(g78,g70)
    c: PointOnObject(g78,g71)
    c: Tangent(g70,g77) = -1.5708
    c: Tangent(g71,g77) = -1.5708
    c: PointOnObject(g80,g72)
    c: PointOnObject(g80,g69)
    c: Tangent(g72,g79) = -1.5708
    c: Tangent(g69,g79) = -1.5708
    c: Equal(g79,g73)
    c: Equal(g73,g77)
    c: Equal(g77,g75)
    c: Equal(g70,g71)
    c: Symmetric(g71,g71,g82)
    c: Symmetric(g69,g69,g82)
    c: Symmetric(g72,g72,g83)
    c: Symmetric(g70,g70,g83)
    c: PointOnObject(g81,g82)
    c: PointOnObject(g81,g83)
    c: Equal(g73,g43)
    c: Equal(g43,g58)
    c: Equal(g58,g4)
    c: Equal(g82,g52)
    c: Equal(g52,g67)
    c: Equal(g67,g13)
    c: Coincident(g51,g16)
    c: Coincident(g66,g21)
    c: Coincident(g12,g20)
    c: Horizontal(g84)
    c: Horizontal(g86)
    c: Vertical(g85)
    c: Vertical(g87)
    c: PointOnObject(g89,g86)
    c: PointOnObject(g89,g87)
    c: Tangent(g86,g88) = -1.5708
    c: Tangent(g87,g88) = -1.5708
    c: PointOnObject(g91,g85)
    c: PointOnObject(g91,g84)
    c: Tangent(g85,g90) = -1.5708
    c: Tangent(g84,g90) = -1.5708
    c: PointOnObject(g93,g85)
    c: PointOnObject(g93,g86)
    c: Tangent(g85,g92) = -1.5708
    c: Tangent(g86,g92) = -1.5708
    c: PointOnObject(g95,g87)
    c: PointOnObject(g95,g84)
    c: Tangent(g87,g94) = -1.5708
    c: Tangent(g84,g94) = -1.5708
    c: Equal(g94,g88)
    c: Equal(g88,g92)
    c: Equal(g92,g90)
    c: Equal(g85,g86)
    c: Symmetric(g86,g86,g97)
    c: Symmetric(g84,g84,g97)
    c: Symmetric(g87,g87,g98)
    c: Symmetric(g85,g85,g98)
    c: PointOnObject(g96,g97)
    c: PointOnObject(g96,g98)
    c: Horizontal(g99)
    c: Horizontal(g101)
    c: Vertical(g100)
    c: Vertical(g102)
    c: PointOnObject(g104,g101)
    c: PointOnObject(g104,g102)
    c: Tangent(g101,g103) = -1.5708
    c: Tangent(g102,g103) = -1.5708
    c: PointOnObject(g106,g100)
    c: PointOnObject(g106,g99)
    c: Tangent(g100,g105) = -1.5708
    c: Tangent(g99,g105) = -1.5708
    c: PointOnObject(g108,g100)
    c: PointOnObject(g108,g101)
    c: Tangent(g100,g107) = -1.5708
    c: Tangent(g101,g107) = -1.5708
    c: PointOnObject(g110,g102)
    c: PointOnObject(g110,g99)
    c: Tangent(g102,g109) = -1.5708
    c: Tangent(g99,g109) = -1.5708
    c: Equal(g109,g103)
    c: Equal(g103,g107)
    c: Equal(g107,g105)
    c: Equal(g100,g101)
    c: Symmetric(g101,g101,g112)
    c: Symmetric(g99,g99,g112)
    c: Symmetric(g102,g102,g113)
    c: Symmetric(g100,g100,g113)
    c: PointOnObject(g111,g112)
    c: PointOnObject(g111,g113)
    c: Horizontal(g114)
    c: Horizontal(g116)
    c: Vertical(g115)
    c: Vertical(g117)
    c: PointOnObject(g119,g116)
    c: PointOnObject(g119,g117)
    c: Tangent(g116,g118) = -1.5708
    c: Tangent(g117,g118) = -1.5708
    c: PointOnObject(g121,g115)
    c: PointOnObject(g121,g114)
    c: Tangent(g115,g120) = -1.5708
    c: Tangent(g114,g120) = -1.5708
    c: PointOnObject(g123,g115)
    c: PointOnObject(g123,g116)
    c: Tangent(g115,g122) = -1.5708
    c: Tangent(g116,g122) = -1.5708
    c: PointOnObject(g125,g117)
    c: PointOnObject(g125,g114)
    c: Tangent(g117,g124) = -1.5708
    c: Tangent(g114,g124) = -1.5708
    c: Equal(g124,g118)
    c: Equal(g118,g122)
    c: Equal(g122,g120)
    c: Equal(g115,g116)
    c: Symmetric(g116,g116,g127)
    c: Symmetric(g114,g114,g127)
    c: Symmetric(g117,g117,g128)
    c: Symmetric(g115,g115,g128)
    c: PointOnObject(g126,g127)
    c: PointOnObject(g126,g128)
    c: Horizontal(g129)
    c: Horizontal(g131)
    c: Vertical(g130)
    c: Vertical(g132)
    c: PointOnObject(g134,g131)
    c: PointOnObject(g134,g132)
    c: Tangent(g131,g133) = -1.5708
    c: Tangent(g132,g133) = -1.5708
    c: PointOnObject(g136,g130)
    c: PointOnObject(g136,g129)
    c: Tangent(g130,g135) = -1.5708
    c: Tangent(g129,g135) = -1.5708
    c: PointOnObject(g138,g130)
    c: PointOnObject(g138,g131)
    c: Tangent(g130,g137) = -1.5708
    c: Tangent(g131,g137) = -1.5708
    c: PointOnObject(g140,g132)
    c: PointOnObject(g140,g129)
    c: Tangent(g132,g139) = -1.5708
    c: Tangent(g129,g139) = -1.5708
    c: Equal(g139,g133)
    c: Equal(g133,g137)
    c: Equal(g137,g135)
    c: Equal(g130,g131)
    c: Symmetric(g131,g131,g142)
    c: Symmetric(g129,g129,g142)
    c: Symmetric(g132,g132,g143)
    c: Symmetric(g130,g130,g143)
    c: PointOnObject(g141,g142)
    c: PointOnObject(g141,g143)
    c: Equal(g133,g118)
    c: Equal(g118,g103)
    c: Equal(g103,g88)
    c: Equal(g88,g73)
    c: Equal(g142,g127)
    c: Equal(g127,g112)
    c: Equal(g112,g97)
    c: Equal(g97,g82)
    c: Coincident(g126,g15)
    c: Coincident(g111,g15)
    c: Coincident(g96,g19)
    c: Coincident(g81,g19)
    c: Horizontal(g144)
    c: Horizontal(g146)
    c: Vertical(g145)
    c: Vertical(g147)
    c: PointOnObject(g149,g146)
    c: PointOnObject(g149,g147)
    c: Tangent(g146,g148) = -1.5708
    c: Tangent(g147,g148) = -1.5708
    c: PointOnObject(g151,g145)
    c: PointOnObject(g151,g144)
    c: Tangent(g145,g150) = -1.5708
    c: Tangent(g144,g150) = -1.5708
    c: PointOnObject(g153,g145)
    c: PointOnObject(g153,g146)
    c: Tangent(g145,g152) = -1.5708
    c: Tangent(g146,g152) = -1.5708
    c: PointOnObject(g155,g147)
    c: PointOnObject(g155,g144)
    c: Tangent(g147,g154) = -1.5708
    c: Tangent(g144,g154) = -1.5708
    c: Equal(g154,g148)
    c: Equal(g148,g152)
    c: Equal(g152,g150)
    c: Equal(g145,g146)
    c: Symmetric(g146,g146,g157)
    c: Symmetric(g144,g144,g157)
    c: Symmetric(g147,g147,g158)
    c: Symmetric(g145,g145,g158)
    c: PointOnObject(g156,g157)
    c: PointOnObject(g156,g158)
    c: Horizontal(g159)
    c: Horizontal(g161)
    c: Vertical(g160)
    c: Vertical(g162)
    c: PointOnObject(g164,g161)
    c: PointOnObject(g164,g162)
    c: Tangent(g161,g163) = -1.5708
    c: Tangent(g162,g163) = -1.5708
    c: PointOnObject(g166,g160)
    c: PointOnObject(g166,g159)
    c: Tangent(g160,g165) = -1.5708
    c: Tangent(g159,g165) = -1.5708
    c: PointOnObject(g168,g160)
    c: PointOnObject(g168,g161)
    c: Tangent(g160,g167) = -1.5708
    c: Tangent(g161,g167) = -1.5708
    c: PointOnObject(g170,g162)
    c: PointOnObject(g170,g159)
    c: Tangent(g162,g169) = -1.5708
    c: Tangent(g159,g169) = -1.5708
    c: Equal(g169,g163)
    c: Equal(g163,g167)
    c: Equal(g167,g165)
    c: Equal(g160,g161)
    c: Symmetric(g161,g161,g172)
    c: Symmetric(g159,g159,g172)
    c: Symmetric(g162,g162,g173)
    c: Symmetric(g160,g160,g173)
    c: PointOnObject(g171,g172)
    c: PointOnObject(g171,g173)
    c: Horizontal(g174)
    c: Horizontal(g176)
    c: Vertical(g175)
    c: Vertical(g177)
    c: PointOnObject(g179,g176)
    c: PointOnObject(g179,g177)
    c: Tangent(g176,g178) = -1.5708
    c: Tangent(g177,g178) = -1.5708
    c: PointOnObject(g181,g175)
    c: PointOnObject(g181,g174)
    c: Tangent(g175,g180) = -1.5708
    c: Tangent(g174,g180) = -1.5708
    c: PointOnObject(g183,g175)
    c: PointOnObject(g183,g176)
    c: Tangent(g175,g182) = -1.5708
    c: Tangent(g176,g182) = -1.5708
    c: PointOnObject(g185,g177)
    c: PointOnObject(g185,g174)
    c: Tangent(g177,g184) = -1.5708
    c: Tangent(g174,g184) = -1.5708
    c: Equal(g184,g178)
    c: Equal(g178,g182)
    c: Equal(g182,g180)
    c: Equal(g175,g176)
    c: Symmetric(g176,g176,g187)
    c: Symmetric(g174,g174,g187)
    c: Symmetric(g177,g177,g188)
    c: Symmetric(g175,g175,g188)
    c: PointOnObject(g186,g187)
    c: PointOnObject(g186,g188)
    c: Horizontal(g189)
    c: Horizontal(g191)
    c: Vertical(g190)
    c: Vertical(g192)
    c: PointOnObject(g194,g191)
    c: PointOnObject(g194,g192)
    c: Tangent(g191,g193) = -1.5708
    c: Tangent(g192,g193) = -1.5708
    c: PointOnObject(g196,g190)
    c: PointOnObject(g196,g189)
    c: Tangent(g190,g195) = -1.5708
    c: Tangent(g189,g195) = -1.5708
    c: PointOnObject(g198,g190)
    c: PointOnObject(g198,g191)
    c: Tangent(g190,g197) = -1.5708
    c: Tangent(g191,g197) = -1.5708
    c: PointOnObject(g200,g192)
    c: PointOnObject(g200,g189)
    c: Tangent(g192,g199) = -1.5708
    c: Tangent(g189,g199) = -1.5708
    c: Equal(g199,g193)
    c: Equal(g193,g197)
    c: Equal(g197,g195)
    c: Equal(g190,g191)
    c: Symmetric(g191,g191,g202)
    c: Symmetric(g189,g189,g202)
    c: Symmetric(g192,g192,g203)
    c: Symmetric(g190,g190,g203)
    c: PointOnObject(g201,g202)
    c: PointOnObject(g201,g203)
    c: Equal(g202,g187)
    c: Equal(g187,g172)
    c: Equal(g172,g157)
    c: Equal(g157,g142)
    c: Equal(g193,g178)
    c: Equal(g178,g163)
    c: Equal(g163,g148)
    c: Equal(g148,g133)
    c: Coincident(g186,g25)
    c: Coincident(g171,g27)
    c: Coincident(g156,g29)
    c: Coincident(g141,g31)
    c: Horizontal(g204)
    c: Horizontal(g206)
    c: Vertical(g205)
    c: Vertical(g207)
    c: PointOnObject(g209,g206)
    c: PointOnObject(g209,g207)
    c: Tangent(g206,g208) = -1.5708
    c: Tangent(g207,g208) = -1.5708
    c: PointOnObject(g211,g205)
    c: PointOnObject(g211,g204)
    c: Tangent(g205,g210) = -1.5708
    c: Tangent(g204,g210) = -1.5708
    c: PointOnObject(g213,g205)
    c: PointOnObject(g213,g206)
    c: Tangent(g205,g212) = -1.5708
    c: Tangent(g206,g212) = -1.5708
    c: PointOnObject(g215,g207)
    c: PointOnObject(g215,g204)
    c: Tangent(g207,g214) = -1.5708
    c: Tangent(g204,g214) = -1.5708
    c: Equal(g214,g208)
    c: Equal(g208,g212)
    c: Equal(g212,g210)
    c: Equal(g205,g206)
    c: Symmetric(g206,g206,g217)
    c: Symmetric(g204,g204,g217)
    c: Symmetric(g207,g207,g218)
    c: Symmetric(g205,g205,g218)
    c: PointOnObject(g216,g217)
    c: PointOnObject(g216,g218)
    c: Horizontal(g219)
    c: Horizontal(g221)
    c: Vertical(g220)
    c: Vertical(g222)
    c: PointOnObject(g224,g221)
    c: PointOnObject(g224,g222)
    c: Tangent(g221,g223) = -1.5708
    c: Tangent(g222,g223) = -1.5708
    c: PointOnObject(g226,g220)
    c: PointOnObject(g226,g219)
    c: Tangent(g220,g225) = -1.5708
    c: Tangent(g219,g225) = -1.5708
    c: PointOnObject(g228,g220)
    c: PointOnObject(g228,g221)
    c: Tangent(g220,g227) = -1.5708
    c: Tangent(g221,g227) = -1.5708
    c: PointOnObject(g230,g222)
    c: PointOnObject(g230,g219)
    c: Tangent(g222,g229) = -1.5708
    c: Tangent(g219,g229) = -1.5708
    c: Equal(g229,g223)
    c: Equal(g223,g227)
    c: Equal(g227,g225)
    c: Equal(g220,g221)
    c: Symmetric(g221,g221,g232)
    c: Symmetric(g219,g219,g232)
    c: Symmetric(g222,g222,g233)
    c: Symmetric(g220,g220,g233)
    c: PointOnObject(g231,g232)
    c: PointOnObject(g231,g233)
    c: Horizontal(g234)
    c: Horizontal(g236)
    c: Vertical(g235)
    c: Vertical(g237)
    c: PointOnObject(g239,g236)
    c: PointOnObject(g239,g237)
    c: Tangent(g236,g238) = -1.5708
    c: Tangent(g237,g238) = -1.5708
    c: PointOnObject(g241,g235)
    c: PointOnObject(g241,g234)
    c: Tangent(g235,g240) = -1.5708
    c: Tangent(g234,g240) = -1.5708
    c: PointOnObject(g243,g235)
    c: PointOnObject(g243,g236)
    c: Tangent(g235,g242) = -1.5708
    c: Tangent(g236,g242) = -1.5708
    c: PointOnObject(g245,g237)
    c: PointOnObject(g245,g234)
    c: Tangent(g237,g244) = -1.5708
    c: Tangent(g234,g244) = -1.5708
    c: Equal(g244,g238)
    c: Equal(g238,g242)
    c: Equal(g242,g240)
    c: Equal(g235,g236)
    c: Symmetric(g236,g236,g247)
    c: Symmetric(g234,g234,g247)
    c: Symmetric(g237,g237,g248)
    c: Symmetric(g235,g235,g248)
    c: PointOnObject(g246,g247)
    c: PointOnObject(g246,g248)
    c: Horizontal(g249)
    c: Horizontal(g251)
    c: Vertical(g250)
    c: Vertical(g252)
    c: PointOnObject(g254,g251)
    c: PointOnObject(g254,g252)
    c: Tangent(g251,g253) = -1.5708
    c: Tangent(g252,g253) = -1.5708
    c: PointOnObject(g256,g250)
    c: PointOnObject(g256,g249)
    c: Tangent(g250,g255) = -1.5708
    c: Tangent(g249,g255) = -1.5708
    c: PointOnObject(g258,g250)
    c: PointOnObject(g258,g251)
    c: Tangent(g250,g257) = -1.5708
    c: Tangent(g251,g257) = -1.5708
    c: PointOnObject(g260,g252)
    c: PointOnObject(g260,g249)
    c: Tangent(g252,g259) = -1.5708
    c: Tangent(g249,g259) = -1.5708
    c: Equal(g259,g253)
    c: Equal(g253,g257)
    c: Equal(g257,g255)
    c: Equal(g250,g251)
    c: Diameter(g253) = 4.2
    c: Symmetric(g251,g251,g262)
    c: Symmetric(g249,g249,g262)
    c: Symmetric(g252,g252,g263)
    c: Symmetric(g250,g250,g263)
    c: PointOnObject(g261,g262)
    c: PointOnObject(g261,g263)
    c: DistanceY(g262,g262) = 17
    c: Equal(g262,g247)
    c: Equal(g247,g232)
    c: Equal(g232,g217)
    c: Equal(g217,g202)
    c: Equal(g253,g238)
    c: Equal(g238,g223)
    c: Equal(g223,g208)
    c: Equal(g208,g193)
    c: Coincident(g246,g25)
    c: Coincident(g231,g26)
    c: Coincident(g216,g29)
    c: Coincident(g201,g30)
    c: Coincident(g261,g17)
FEATURE [PartDesign::Pocket] Pocket001
  BaseFeature = -> Clone001
  Direction = (0,0,-1)
  Length = 5
  Length2 = 5
  Profile = -> Sketch008
  ReferenceAxis = -> Sketch008 [N_Axis]
  Refine = true
  Suppressed = false
  Type = 1
FEATURE [PartDesign::Body] Body002  label="FRONTPANEL-SHEET-BU16"
  AllowCompound = false
  BaseFeature = -> Body
  Group = -> [Clone001,Sketch005,Sketch006,Sketch007,Sketch008,Pocket001]
  Origin = -> Origin002
  Tip = -> Pocket001
FEATURE [TechDraw::DrawViewPart] View  label="View 1"
  CoarseView = false
  Direction = (0,0,1)
  Focus = 100
  HardHidden = false
  IsoCount = 0
  IsoHidden = false
  IsoVisible = false
  LockPosition = false
  Perspective = false
  Rotation = 0
  ScaleType = 2
  ScrubCount = 0
  SeamHidden = false
  SeamVisible = false
  SmoothHidden = false
  SmoothVisible = true
  Source = -> [Body002]
  X = 93.8022
  XDirection = (1,0,0)
  Y = 200.975
FEATURE [TechDraw::DrawViewPart] View002  label="View 2"
  CoarseView = false
  Direction = (-1,0,0)
  Focus = 100
  HardHidden = true
  IsoCount = 0
  IsoHidden = false
  IsoVisible = false
  LockPosition = false
  Perspective = false
  Rotation = 0
  ScaleType = 0
  ScrubCount = 0
  SeamHidden = false
  SeamVisible = false
  SmoothHidden = false
  SmoothVisible = true
  Source = -> [Body002]
  X = 198.963
  XDirection = (0,0,1)
  Y = 203.985
FEATURE [TechDraw::DrawViewPart] View003  label="View 3"
  CoarseView = false
  Direction = (-0.57735,-0.57735,0.57735)
  Focus = 100
  HardHidden = false
  IsoCount = 0
  IsoHidden = false
  IsoVisible = false
  LockPosition = false
  Perspective = false
  Rotation = 0
  Scale = 0.5
  ScaleType = 2
  ScrubCount = 0
  SeamHidden = false
  SeamVisible = false
  SmoothHidden = false
  SmoothVisible = true
  Source = -> [Body002]
  X = 382.784
  XDirection = (-0.707107,5.7735e-07,-0.707107)
  Y = 152.399
FEATURE [TechDraw::DrawViewBalloon] Balloon007
  BubbleShape = 6
  EndType = 6
  EndTypeScale = 1
  KinkLength = -0.1
  LockPosition = false
  OriginX = 0.520628
  OriginY = 38.9805
  Rotation = 0
  ScaleType = 0
  ShapeScale = 1
  SourceView = -> View002
  Text = A
  TextWrapLen = -1
  X = 13.2545
  Y = 38.9634
FEATURE [TechDraw::DrawViewBalloon] Balloon009
  BubbleShape = 6
  EndType = 0
  EndTypeScale = 1
  KinkLength = -0.1
  LockPosition = false
  OriginX = 0.859808
  OriginY = -26.8614
  Rotation = 0
  ScaleType = 0
  ShapeScale = 1
  SourceView = -> View002
  Text = ⏥|0,2
  TextWrapLen = -1
  X = 24.6858
  Y = -26.8434
FEATURE [TechDraw::DrawViewBalloon] Balloon012
  BubbleShape = 6
  EndType = 6
  EndTypeScale = 1
  KinkLength = 0
  LockPosition = false
  OriginX = -18.185
  OriginY = -40.005
  Rotation = 0
  ScaleType = 0
  ShapeScale = 1
  SourceView = -> View
  Text = ⌖|⌀0,15|A|B|C
  TextWrapLen = -1
  X = 6.52725
  Y = -75.2914
FEATURE [TechDraw::DrawViewBalloon] Balloon013
  BubbleShape = 6
  EndType = 6
  EndTypeScale = 1
  KinkLength = 0
  LockPosition = false
  OriginX = -18.185
  OriginY = -40.005
  Rotation = 0
  ScaleType = 0
  ShapeScale = 1
  SourceView = -> View
  Text = ○|0,1
  TextWrapLen = -1
  X = -11.3647
  Y = -85.9016
FEATURE [TechDraw::DrawViewBalloon] Balloon016
  BubbleShape = 6
  EndType = 6
  EndTypeScale = 1
  KinkLength = 0
  LockPosition = false
  OriginX = 11.835
  OriginY = -31.505
  Rotation = 0
  ScaleType = 0
  ShapeScale = 1
  SourceView = -> View
  Text = ⌖|⌀0,15|A|B|C
  TextWrapLen = -1
  X = 75.4647
  Y = -84.3926
FEATURE [TechDraw::DrawViewDimension] Dimension
  AngleOverride = false
  Arbitrary = false
  ArbitraryTolerances = false
  EqualTolerance = true
  ExtensionAngle = 0
  FormatSpec = 16x ⌀%.2w
  FormatSpecOverTolerance = %+.2w
  FormatSpecUnderTolerance = %+.2w
  Inverted = false
  LineAngle = 0
  LockPosition = false
  MeasureType = 1
  OverTolerance = 0.05
  References2D = -> [View]
  Rotation = 0
  ScaleType = 0
  TheoreticalExact = false
  Type = 5
  UnderTolerance = -0.05
  X = 63.7674
  Y = -73.6022
FEATURE [TechDraw::DrawHatch] Hatch  label="HatchF1"
  HatchPattern = C:/Program Files/FreeCAD 0.21/data/Mod/TechDraw/Patterns/solid.svg
  Source = -> View003 [Face1]
FEATURE [TechDraw::DrawViewDimension] Dimension010
  AngleOverride = false
  Arbitrary = false
  ArbitraryTolerances = false
  EqualTolerance = false
  ExtensionAngle = 0
  FormatSpec = %.2w
  FormatSpecOverTolerance = %+.2w
  FormatSpecUnderTolerance = %+.2w
  Inverted = false
  LineAngle = 0
  LockPosition = false
  MeasureType = 1
  OverTolerance = 0
  References2D = -> [View]
  Rotation = 0
  ScaleType = 0
  TheoreticalExact = false
  Type = 2
  UnderTolerance = -0.2
  X = 64.3064
  Y = -0.75489
FEATURE [TechDraw::DrawViewPart] View004
  CoarseView = false
  Direction = (0,0,-1)
  Focus = 100
  HardHidden = true
  IsoCount = 0
  IsoHidden = false
  IsoVisible = false
  LockPosition = false
  Perspective = false
  Rotation = 0
  ScaleType = 0
  ScrubCount = 0
  SeamHidden = false
  SeamVisible = true
  SmoothHidden = false
  SmoothVisible = true
  Source = -> [Body002]
  X = 297.303
  XDirection = (-1,-1e-06,0)
  Y = 200.441
FEATURE [TechDraw::DrawViewDimension] Dimension011
  AngleOverride = false
  Arbitrary = false
  ArbitraryTolerances = false
  EqualTolerance = false
  ExtensionAngle = 0
  FormatSpec = %.2w
  FormatSpecOverTolerance = %+.2w
  FormatSpecUnderTolerance = %+.2w
  Inverted = false
  LineAngle = 0
  LockPosition = false
  MeasureType = 1
  OverTolerance = 0
  References2D = -> [View004]
  Rotation = 0
  ScaleType = 0
  TheoreticalExact = false
  Type = 1
  UnderTolerance = -0.2
  X = -0.499889
  Y = 65.7969
FEATURE [TechDraw::DrawViewBalloon] Balloon022
  BubbleShape = 6
  EndType = 6
  EndTypeScale = 1
  KinkLength = -0.1
  LockPosition = false
  OriginX = -52.2651
  OriginY = 58.6802
  Rotation = 0
  ScaleType = 0
  ShapeScale = 1
  SourceView = -> Dimension011
  Text = B
  TextWrapLen = -1
  X = -62.1979
  Y = 58.6576
FEATURE [TechDraw::DrawViewDimension] Dimension013
  AngleOverride = false
  Arbitrary = false
  ArbitraryTolerances = true
  BoxCorners = (2) [(-52.175,-52.175,0),(52.175,52.175,0)]
  EqualTolerance = false
  ExtensionAngle = 0
  FormatSpec = 16x ⌀%.2w
  FormatSpecOverTolerance = +0,15
  FormatSpecUnderTolerance = 0
  Inverted = false
  LineAngle = 0
  LockPosition = false
  MeasureType = 1
  OverTolerance = 0
  References2D = -> [View]
  Rotation = 0
  ScaleType = 0
  TheoreticalExact = false
  Type = 5
  UnderTolerance = 0
  X = -11.0501
  Y = -62.5809
FEATURE [TechDraw::DrawComplexSection] ComplexSection  label="Section A - A"
  BaseView = -> View
  Caption = Section A-A
  CoarseView = false
  CutSurfaceDisplay = 2
  CuttingToolWireObject = -> Sketch007
  Direction = (1e-16,-1,0)
  FileGeomPattern = C:/Program Files/FreeCAD 0.21/data/Mod/TechDraw/PAT/FCPAT.pat
  FileHatchPattern = C:/Program Files/FreeCAD 0.21/data/Mod/TechDraw/Patterns/simple.svg
  Focus = 100
  FuseBeforeCut = false
  HardHidden = true
  HatchOffset = (0,0,0)
  HatchRotation = 0
  HatchScale = 1
  IsoCount = 0
  IsoHidden = false
  IsoVisible = false
  LockPosition = false
  NameGeomPattern = Gyémánt bevonatú
  Perspective = false
  ProjectionStrategy = 1
  Rotation = 0
  Scale = 10
  ScaleType = 2
  ScrubCount = 0
  SeamHidden = false
  SeamVisible = true
  SectionDirection = 4
  SectionLineStretch = 1
  SectionNormal = (1e-16,-1,0)
  SectionOrigin = (0,0,0)
  SectionSymbol = A
  SmoothHidden = false
  SmoothVisible = true
  Source = -> [Body002]
  TrimAfterCut = false
  UsePreviousCut = false
  X = 79.5678
  XDirection = (1,1e-16,0)
  Y = 64.2074
FEATURE [TechDraw::DrawViewBalloon] Balloon023
  BubbleShape = 1
  EndType = 0
  EndTypeScale = 1
  KinkLength = -0.1
  LockPosition = false
  OriginX = -52.0652
  OriginY = 52.0652
  Rotation = 0
  ScaleType = 0
  ShapeScale = 1
  SourceView = -> View
  Text = 4x R0,38
  TextWrapLen = -1
  X = -70.0132
  Y = 68.6837
FEATURE [TechDraw::DrawViewDimension] Dimension014
  AngleOverride = false
  Arbitrary = false
  ArbitraryTolerances = false
  EqualTolerance = true
  ExtensionAngle = 0
  FormatSpec = %.2w
  FormatSpecOverTolerance = %+.2w
  FormatSpecUnderTolerance = %+.2w
  Inverted = false
  LineAngle = 0
  LockPosition = false
  MeasureType = 1
  OverTolerance = 0
  References2D = -> [ComplexSection]
  Rotation = 0
  ScaleType = 0
  TheoreticalExact = false
  Type = 6
  UnderTolerance = 0
  X = -27.7612
  Y = 28.1448
FEATURE [TechDraw::DrawViewDimension] Dimension015
  AngleOverride = false
  Arbitrary = false
  ArbitraryTolerances = false
  EqualTolerance = true
  ExtensionAngle = 0
  FormatSpec = 4x ⌀%.2w
  FormatSpecOverTolerance = %+.2w
  FormatSpecUnderTolerance = %+.2w
  Inverted = false
  LineAngle = 0
  LockPosition = false
  MeasureType = 1
  OverTolerance = 0
  References2D = -> [ComplexSection]
  Rotation = 0
  ScaleType = 0
  TheoreticalExact = false
  Type = 1
  UnderTolerance = 0
  X = 24.0105
  Y = 22.4679
FEATURE [TechDraw::DrawViewDimension] Dimension016
  AngleOverride = false
  Arbitrary = false
  ArbitraryTolerances = false
  EqualTolerance = true
  ExtensionAngle = 0
  FormatSpec = 4x ⌀%.2w
  FormatSpecOverTolerance = %+.2w
  FormatSpecUnderTolerance = %+.2w
  Inverted = false
  LineAngle = 0
  LockPosition = false
  MeasureType = 1
  OverTolerance = 0.05
  References2D = -> [ComplexSection]
  Rotation = 0
  ScaleType = 0
  TheoreticalExact = false
  Type = 1
  UnderTolerance = -0.05
  X = 52.1239
  Y = -3.38615
FEATURE [TechDraw::DrawViewDimension] Dimension017
  AngleOverride = false
  Arbitrary = false
  ArbitraryTolerances = false
  EqualTolerance = true
  ExtensionAngle = 0
  FormatSpec = (%.2w)
  FormatSpecOverTolerance = %+.2w
  FormatSpecUnderTolerance = %+.2w
  Inverted = false
  LineAngle = 0
  LockPosition = false
  MeasureType = 1
  OverTolerance = 0
  References2D = -> [ComplexSection]
  Rotation = 0
  ScaleType = 0
  TheoreticalExact = false
  Type = 2
  UnderTolerance = 0
  X = -38.4382
  Y = 1.69271
FEATURE [TechDraw::DrawViewBalloon] Balloon024
  BubbleShape = 6
  EndType = 6
  EndTypeScale = 1
  KinkLength = 0
  LockPosition = false
  OriginX = 48.1576
  OriginY = -16.4662
  Rotation = 0
  ScaleType = 0
  ShapeScale = 1
  SourceView = -> Dimension016
  Text = ⌖|⌀0,15|A|B|C
  TextWrapLen = -1
  X = 62.263
  Y = -14.1919
FEATURE [TechDraw::DrawViewBalloon] Balloon027
  BubbleShape = 1
  EndType = 0
  EndTypeScale = 1
  KinkLength = 0
  LockPosition = false
  OriginX = 0.686504
  OriginY = -44.4808
  Rotation = 0
  ScaleType = 0
  ShapeScale = 1
  SourceView = -> View002
  TextWrapLen = -1
  X = 24.7149
  Y = -70.4411
FEATURE [TechDraw::DrawViewBalloon] Balloon028
  BubbleShape = 1
  EndType = 3
  EndTypeScale = 1
  KinkLength = 0
  LockPosition = false
  OriginX = -6.60818
  OriginY = -22.6738
  Rotation = 0
  ScaleType = 0
  ShapeScale = 1
  SourceView = -> View003
  TextWrapLen = -1
  X = -103.988
  Y = -113.663
FEATURE [TechDraw::DrawHatch] Hatch004  label="Hatch004F51"
  HatchPattern = C:/Program Files/FreeCAD 0.21/data/Mod/TechDraw/Patterns/solid.svg
  Source = -> View003 [Face51,Face37,Face48,Face39]
FEATURE [TechDraw::DrawHatch] Hatch005  label="Hatch005F74"
  HatchPattern = C:/Program Files/FreeCAD 0.21/data/Mod/TechDraw/Patterns/solid.svg
  Source = -> View003 [Face74,Face72,Face80,Face84,Face77,Face91,Face49,Face47,Face45,Face38]
FEATURE [TechDraw::DrawHatch] Hatch006  label="Hatch006F50"
  HatchPattern = C:/Program Files/FreeCAD 0.21/data/Mod/TechDraw/Patterns/solid.svg
  Source = -> View003 [Face50,Face40,Face43,Face44,Face73,Face88,Face87,Face86,Face90]
FEATURE [TechDraw::DrawHatch] Hatch007  label="Hatch007F75"
  HatchPattern = C:/Program Files/FreeCAD 0.21/data/Mod/TechDraw/Patterns/solid.svg
  Source = -> View003 [Face75,Edge184,Face36,Face78,Face42,Face46,Face82,Face41,Face83]
FEATURE [TechDraw::DrawHatch] Hatch008  label="Hatch008F76"
  HatchPattern = C:/Program Files/FreeCAD 0.21/data/Mod/TechDraw/Patterns/solid.svg
  Source = -> View003 [Face76,Face79,Face85,Face81,Face89]
FEATURE [TechDraw::DrawHatch] Hatch009  label="Hatch009F3"
  HatchPattern = C:/Program Files/FreeCAD 0.21/data/Mod/TechDraw/Patterns/solid.svg
  Source = -> View003 [Face3,Face2,Face112]
FEATURE [TechDraw::DrawViewBalloon] Balloon
  BubbleShape = 6
  EndType = 6
  EndTypeScale = 1
  KinkLength = -0.1
  LockPosition = false
  OriginX = 72.942
  OriginY = 52.209
  Rotation = 0
  ScaleType = 0
  ShapeScale = 1
  SourceView = -> Balloon012
  Text = C
  TextWrapLen = -1
  X = 73.2859
  Y = 62.7848
FEATURE [TechDraw::DrawViewBalloon] Balloon029
  BubbleShape = 2
  EndType = 6
  EndTypeScale = 1
  KinkLength = 0
  LockPosition = false
  OriginX = 16.1649
  OriginY = -66.3393
  Rotation = 0
  ScaleType = 0
  ShapeScale = 1
  SourceView = -> View
  Text = 3
  TextWrapLen = -1
  X = 19.1544
  Y = -63.5015
FEATURE [TechDraw::DrawPage] Page003  label="BU16_Drawing"
  KeepUpdated = true
  NextBalloonIndex = 39
  ProjectionType = 0
  Template = -> Template003
  Views = -> [View,View002,View003,Balloon007,Balloon009,Balloon012,Balloon013,Balloon016,Dimension,Dimension010,View004,Dimension011,Balloon022,Dimension013,ComplexSection,Balloon023,Dimension014,Dimension015,Dimension016,Dimension017,Balloon024,Annotation002,Balloon026,Balloon027,Balloon028,Annotation,Annotation001,Balloon,Balloon029]
